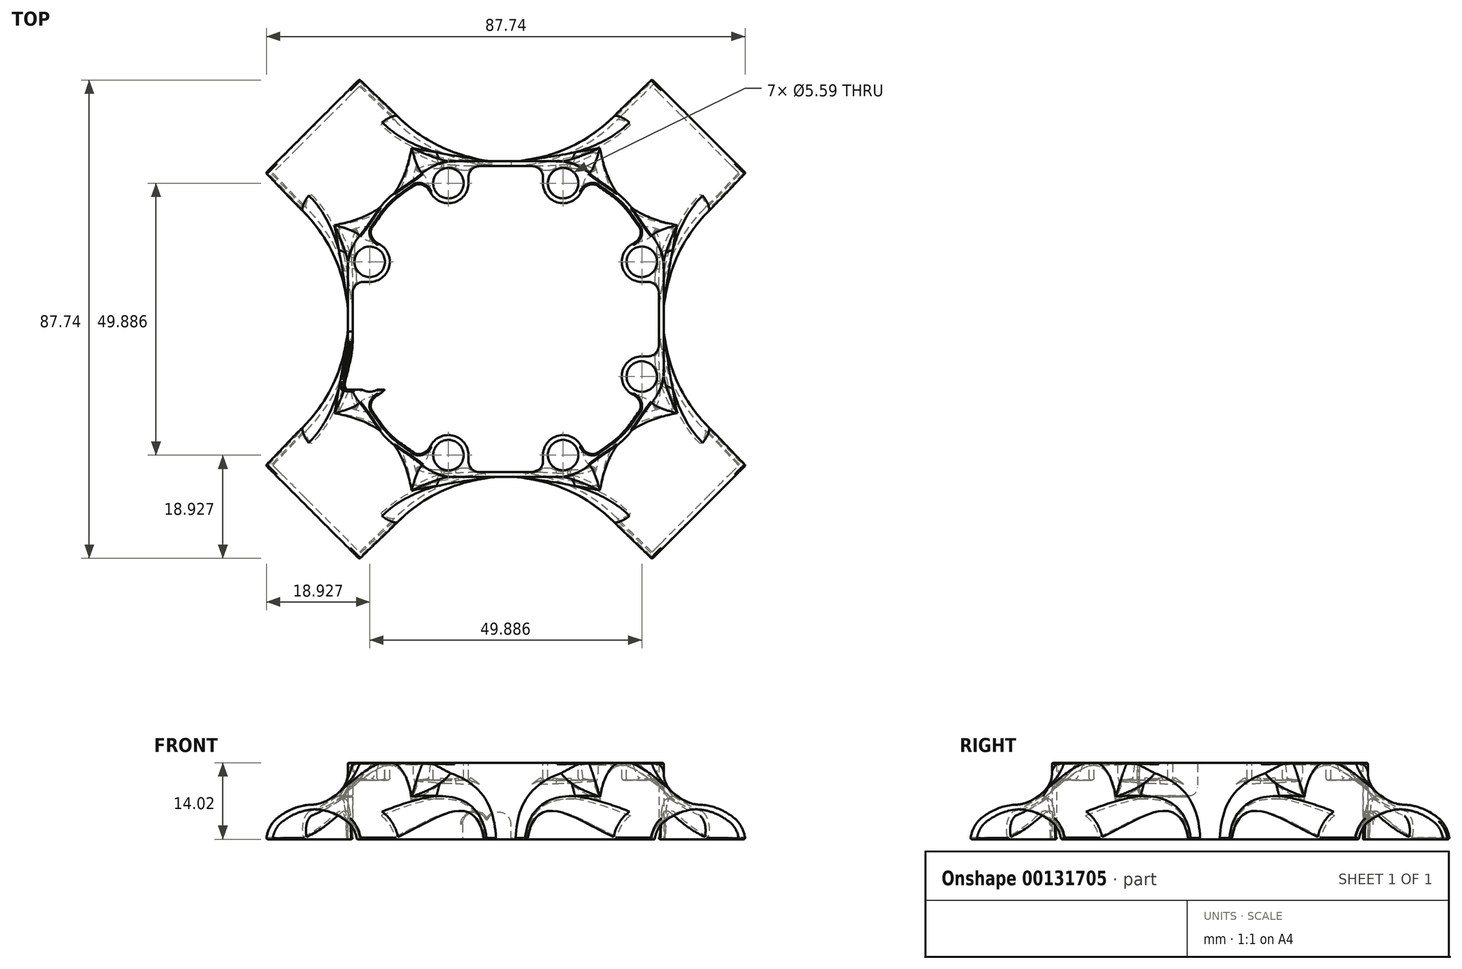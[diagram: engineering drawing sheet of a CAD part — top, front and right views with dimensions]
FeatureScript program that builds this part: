
annotation { "Feature Type Name" : "Feature", "Feature Type Description" : "" }
export const myFeature = defineFeature(function(context is Context, id is Id, definition is map)
    precondition{}
    {
        {
            var Q0;
            Q0=qCreatedBy(makeId("Top.planeOp"),FACE);
            var sketch = newSketch(context, id + "F0", { "sketchPlane" : qUnion([Q0])});
            skLineSegment(sketch, "E0.left", {"start": v(28.96, 12.57) * mm, "end": v(28.96, -12.57) * mm});
            skLineSegment(sketch, "E0.right", {"start": v(-28.96, 12.57) * mm, "end": v(-28.96, -12.57) * mm});
            skPoint(sketch, "E0.middle", {"position": v(0, 0) * mm});
            skLineSegment(sketch, "E1.bottom", {"start": v(12.57, 28.96) * mm, "end": v(-12.57, 28.96) * mm});
            skLineSegment(sketch, "E1.top", {"start": v(12.57, -28.96) * mm, "end": v(-12.57, -28.96) * mm});
            skArc(sketch, "E2", {"start": v(-28.96, 12.57) * mm, "mid": v(-20.01, 20.01) * mm, "end": v(-12.57, 28.96) * mm});
            skArc(sketch, "E3", {"start": v(12.57, 28.96) * mm, "mid": v(20.01, 20.01) * mm, "end": v(28.96, 12.57) * mm});
            skArc(sketch, "E4", {"start": v(28.96, -12.57) * mm, "mid": v(20.01, -20.01) * mm, "end": v(12.57, -28.96) * mm});
            skArc(sketch, "E5", {"start": v(-12.57, -28.96) * mm, "mid": v(-20.01, -20.01) * mm, "end": v(-28.96, -12.57) * mm});
            skSolve(sketch);
        }
        {
            var Q0;
            Q0=qCreatedBy(makeId("Top.planeOp"),FACE);
            cPlane(context, id + "F1", {"entities" : qUnion([Q0]), "cplaneType" : CPlaneType.OFFSET, "offset" : 14.02 * mm, "oppositeDirection" : true, "width" : 152.4 * mm, "height" : 152.4 * mm});
        }
        {
            var Q0;
            Q0=qCreatedBy(id+"F1.planeOp",FACE);
            var sketch = newSketch(context, id + "F2", { "sketchPlane" : qUnion([Q0])});
            skPoint(sketch, "E6.middle", {"position": v(0, 0) * mm});
            skArc(sketch, "E7", {"start": v(-37.14, -19.76) * mm, "mid": v(-28.96, 0) * mm, "end": v(-37.14, 19.76) * mm});
            skArc(sketch, "E8", {"start": v(-19.76, 37.14) * mm, "mid": v(0, 28.96) * mm, "end": v(19.76, 37.14) * mm});
            skArc(sketch, "E9", {"start": v(37.14, 19.76) * mm, "mid": v(28.96, 0) * mm, "end": v(37.14, -19.76) * mm});
            skArc(sketch, "E10", {"start": v(19.76, -37.14) * mm, "mid": v(0, -28.96) * mm, "end": v(-19.76, -37.14) * mm});
            skLineSegment(sketch, "E11", {"start": v(-44.09, 26.7) * mm, "end": v(-37.14, 19.76) * mm});
            skLineSegment(sketch, "E12", {"start": v(-19.76, 37.14) * mm, "end": v(-26.7, 44.09) * mm});
            skLineSegment(sketch, "E13", {"start": v(-26.7, 44.09) * mm, "end": v(-44.09, 26.7) * mm});
            skLineSegment(sketch, "E14", {"start": v(19.76, 37.14) * mm, "end": v(26.7, 44.09) * mm});
            skLineSegment(sketch, "E15", {"start": v(26.7, 44.09) * mm, "end": v(44.09, 26.7) * mm});
            skLineSegment(sketch, "E16", {"start": v(44.09, 26.7) * mm, "end": v(37.14, 19.76) * mm});
            skLineSegment(sketch, "E17", {"start": v(-19.76, -37.14) * mm, "end": v(-26.7, -44.09) * mm});
            skLineSegment(sketch, "E18", {"start": v(-26.7, -44.09) * mm, "end": v(-44.09, -26.7) * mm});
            skLineSegment(sketch, "E19", {"start": v(-44.09, -26.7) * mm, "end": v(-37.14, -19.76) * mm});
            skLineSegment(sketch, "E20", {"start": v(37.14, -19.76) * mm, "end": v(44.09, -26.7) * mm});
            skLineSegment(sketch, "E21", {"start": v(44.09, -26.7) * mm, "end": v(26.7, -44.09) * mm});
            skLineSegment(sketch, "E22", {"start": v(26.7, -44.09) * mm, "end": v(19.76, -37.14) * mm});
            skPoint(sketch, "E23.orphan", {"position": v(-29.11, 29.11) * mm});
            skPoint(sketch, "E24.orphan", {"position": v(29.1, 29.1) * mm});
            skPoint(sketch, "E25.orphan", {"position": v(29.11, -29.11) * mm});
            skPoint(sketch, "E26.orphan", {"position": v(-29.1, -29.1) * mm});
            skLineSegment(sketch, "E27.bottom", {"start": v(54.62, -53.7) * mm, "end": v(-54.62, -53.7) * mm});
            skLineSegment(sketch, "E27.top", {"start": v(54.62, 53.7) * mm, "end": v(-54.62, 53.7) * mm});
            skLineSegment(sketch, "E27.left", {"start": v(54.62, -53.7) * mm, "end": v(54.62, 53.7) * mm});
            skLineSegment(sketch, "E27.right", {"start": v(-54.62, -53.7) * mm, "end": v(-54.62, 53.7) * mm});
            skSolve(sketch);
        }
        {
            var Q0;
            Q0=makeQuery(id+"F0.imprint","IMPRINT",FACE,{"disambiguationData":[TD([[makeQuery(id+"F0.imprint","IMPRINT",EDGE,{"derivedFrom":sQuery(id+"F0.wireOp",EDGE,"E0.left")}),-1.0]])]});
            var Q1;
            Q1=qCreatedBy(id+"F1.planeOp",FACE);
            extrude(context, id + "F3", {"entities" : qUnion([Q0]), "endBound" : BoundingType.UP_TO_SURFACE, "oppositeDirection" : true, "endBoundEntityFace" : qUnion([Q1]), "depth" : 25.4 * mm});
        }
        {
            var Q0;
            Q0=makeQuery(id+"F0.imprint","IMPRINT",FACE,{"disambiguationData":[TD([[makeQuery(id+"F0.imprint","IMPRINT",EDGE,{"derivedFrom":sQuery(id+"F0.wireOp",EDGE,"E0.left")}),-1.0]])]});
            extrude(context, id + "F4", {"entities" : qUnion([Q0]), "operationType" : NewBodyOperationType.ADD, "depth" : 25.4 * mm});
        }
        {
            var Q0;
            Q0=qCreatedBy(id+"F1.planeOp",FACE);
            var sketch = newSketch(context, id + "F5", { "sketchPlane" : qUnion([Q0])});
            skLineSegment(sketch, "E28", {"start": v(-26.36, -26.36) * mm, "end": v(26.36, 26.36) * mm});
            skLineSegment(sketch, "E29", {"start": v(26.36, -26.36) * mm, "end": v(-26.36, 26.36) * mm});
            skSolve(sketch);
        }
        {
            var Q0;
            Q0=qCreatedBy(makeId("Front.planeOp"),FACE);
            var Q1;
            Q1=sQuery(id+"F5.wireOp",EDGE,"E28");
            cPlane(context, id + "F6", {"entities" : qUnion([Q0, Q1]), "cplaneType" : CPlaneType.LINE_ANGLE, "offset" : 25.4 * mm, "angle" : 0 * degree, "width" : 152.4 * mm, "height" : 152.4 * mm});
        }
        {
            var Q0;
            Q0=qCreatedBy(makeId("Front.planeOp"),FACE);
            var Q1;
            Q1=sQuery(id+"F5.wireOp",EDGE,"E29");
            cPlane(context, id + "F7", {"entities" : qUnion([Q0, Q1]), "cplaneType" : CPlaneType.LINE_ANGLE, "offset" : 25.4 * mm, "angle" : 0 * degree, "width" : 152.4 * mm, "height" : 152.4 * mm});
        }
        {
            var Q0;
            Q0=qCreatedBy(id+"F6.planeOp",FACE);
            var sketch = newSketch(context, id + "F8", { "sketchPlane" : qUnion([Q0])});
            skCircle(sketch, "E30", {"center": v(50.22, 20.65) * mm, "radius": 28.32 * mm});
            skLineSegment(sketch, "E31.bottom", {"start": v(50.22, 20.65) * mm, "end": v(12.75, 20.65) * mm});
            skLineSegment(sketch, "E31.top", {"start": v(50.22, -14.02) * mm, "end": v(12.75, -14.02) * mm});
            skLineSegment(sketch, "E31.left", {"start": v(50.22, 20.65) * mm, "end": v(50.22, -14.02) * mm});
            skLineSegment(sketch, "E31.right", {"start": v(12.75, 20.65) * mm, "end": v(12.75, -14.02) * mm});
            skCircle(sketch, "E32", {"center": v(-50.22, 20.65) * mm, "radius": 28.32 * mm});
            skLineSegment(sketch, "E33.bottom", {"start": v(-50.22, 20.65) * mm, "end": v(-12.75, 20.65) * mm});
            skLineSegment(sketch, "E33.top", {"start": v(-50.22, -14.02) * mm, "end": v(-12.75, -14.02) * mm});
            skLineSegment(sketch, "E33.left", {"start": v(-50.22, 20.65) * mm, "end": v(-50.22, -14.02) * mm});
            skLineSegment(sketch, "E33.right", {"start": v(-12.75, 20.65) * mm, "end": v(-12.75, -14.02) * mm});
            skSolve(sketch);
        }
        {
            var Q0;
            Q0=qCreatedBy(id+"F7.planeOp",FACE);
            var sketch = newSketch(context, id + "F9", { "sketchPlane" : qUnion([Q0])});
            skCircle(sketch, "E34", {"center": v(-50.22, 20.65) * mm, "radius": 28.32 * mm});
            skCircle(sketch, "E35", {"center": v(50.22, 20.65) * mm, "radius": 28.32 * mm});
            skLineSegment(sketch, "E36.bottom", {"start": v(-50.22, 20.65) * mm, "end": v(-12.75, 20.65) * mm});
            skLineSegment(sketch, "E36.top", {"start": v(-50.22, -14.02) * mm, "end": v(-12.75, -14.02) * mm});
            skLineSegment(sketch, "E36.left", {"start": v(-50.22, 20.65) * mm, "end": v(-50.22, -14.02) * mm});
            skLineSegment(sketch, "E36.right", {"start": v(-12.75, 20.65) * mm, "end": v(-12.75, -14.02) * mm});
            skLineSegment(sketch, "E37.bottom", {"start": v(50.22, 20.65) * mm, "end": v(12.75, 20.65) * mm});
            skLineSegment(sketch, "E37.top", {"start": v(50.22, -14.02) * mm, "end": v(12.75, -14.02) * mm});
            skLineSegment(sketch, "E37.left", {"start": v(50.22, 20.65) * mm, "end": v(50.22, -14.02) * mm});
            skLineSegment(sketch, "E37.right", {"start": v(12.75, 20.65) * mm, "end": v(12.75, -14.02) * mm});
            skSolve(sketch);
        }
        {
            var Q0;
            {var subQ1=sQuery(id+"F8.wireOp",EDGE,"E31.top");Q0=makeQuery(id+"F8.imprint","IMPRINT",FACE,{"disambiguationData":[TD([[makeQuery(id+"F8.imprint","IMPRINT",EDGE,{"derivedFrom":subQ1}),-1.0]])]});}
            var Q1;
            {var subQ1=sQuery(id+"F8.wireOp",EDGE,"E33.top");Q1=makeQuery(id+"F8.imprint","IMPRINT",FACE,{"disambiguationData":[TD([[makeQuery(id+"F8.imprint","IMPRINT",EDGE,{"derivedFrom":subQ1}),1.0]])]});}
            extrude(context, id + "F10", {"entities" : qUnion([Q0, Q1]), "operationType" : NewBodyOperationType.ADD, "endBound" : BoundingType.SYMMETRIC, "depth" : 38.1 * mm});
        }
        {
            var Q0;
            {var subQ1=sQuery(id+"F9.wireOp",EDGE,"E36.top");Q0=makeQuery(id+"F9.imprint","IMPRINT",FACE,{"disambiguationData":[TD([[makeQuery(id+"F9.imprint","IMPRINT",EDGE,{"derivedFrom":subQ1}),1.0]])]});}
            var Q1;
            {var subQ1=sQuery(id+"F9.wireOp",EDGE,"E37.top");Q1=makeQuery(id+"F9.imprint","IMPRINT",FACE,{"disambiguationData":[TD([[makeQuery(id+"F9.imprint","IMPRINT",EDGE,{"derivedFrom":subQ1}),-1.0]])]});}
            extrude(context, id + "F11", {"entities" : qUnion([Q0, Q1]), "operationType" : NewBodyOperationType.ADD, "endBound" : BoundingType.SYMMETRIC, "depth" : 38.1 * mm});
        }
        {
            var Q0;
            Q0=makeQuery(id+"F10.opExtrude","CAP_EDGE",EDGE,{"disambiguationData":[OSD([sQuery(id+"F8.wireOp",EDGE,"E30")])],"isStart":false});
            var Q1;
            Q1=makeQuery(id+"F10.opExtrude","CAP_EDGE",EDGE,{"disambiguationData":[OSD([sQuery(id+"F8.wireOp",EDGE,"E30")])],"isStart":true});
            var Q2;
            Q2=makeQuery(id+"F10.opExtrude","CAP_EDGE",EDGE,{"disambiguationData":[OSD([sQuery(id+"F8.wireOp",EDGE,"E32")])],"isStart":false});
            var Q3;
            Q3=makeQuery(id+"F10.opExtrude","CAP_EDGE",EDGE,{"disambiguationData":[OSD([sQuery(id+"F8.wireOp",EDGE,"E32")])],"isStart":true});
            var Q4;
            Q4=makeQuery(id+"F11.opExtrude","CAP_EDGE",EDGE,{"disambiguationData":[OSD([sQuery(id+"F9.wireOp",EDGE,"E35")])],"isStart":true});
            var Q5;
            Q5=makeQuery(id+"F11.opExtrude","CAP_EDGE",EDGE,{"disambiguationData":[OSD([sQuery(id+"F9.wireOp",EDGE,"E35")])],"isStart":false});
            var Q6;
            Q6=makeQuery(id+"F11.opExtrude","CAP_EDGE",EDGE,{"disambiguationData":[OSD([sQuery(id+"F9.wireOp",EDGE,"E34")])],"isStart":true});
            var Q7;
            Q7=makeQuery(id+"F11.opExtrude","CAP_EDGE",EDGE,{"disambiguationData":[OSD([sQuery(id+"F9.wireOp",EDGE,"E34")])],"isStart":false});
            fillet(context, id + "F12", {"entities" : qUnion([Q0, Q1, Q2, Q3, Q4, Q5, Q6, Q7]), "radius" : 19.05 * mm, "tangentPropagation" : true, "allowEdgeOverflow" : false});
        }
        {
            var Q0;
            Q0=makeQuery(id+"F2.imprint","IMPRINT",FACE,{"disambiguationData":[TD([[makeQuery(id+"F2.imprint","IMPRINT",EDGE,{"derivedFrom":sQuery(id+"F2.wireOp",EDGE,"E7")}),1.0]])]});
            extrude(context, id + "F13", {"entities" : qUnion([Q0]), "operationType" : NewBodyOperationType.REMOVE, "depth" : 50.8 * mm});
        }
        {
            var Q0;
            Q0=makeQuery(id+"F13.boolean.opBoolean","INTERSECT",EDGE,{"derivedFrom":[makeQuery(id+"F12.opFillet","BLEND_FACE",FACE,{"disambiguationData":[OSD([sQuery(id+"F8.wireOp",EDGE,"E30")])]}),makeQuery(id+"F13.opExtrude","SWEPT_FACE",FACE,{"disambiguationData":[OSD([sQuery(id+"F2.wireOp",EDGE,"E19")])]})]});
            var Q1;
            Q1=makeQuery(id+"F13.boolean.opBoolean","INTERSECT",EDGE,{"derivedFrom":[makeQuery(id+"F12.opFillet","BLEND_FACE",FACE,{"disambiguationData":[OSD([sQuery(id+"F8.wireOp",EDGE,"E30")])]}),makeQuery(id+"F13.opExtrude","SWEPT_FACE",FACE,{"disambiguationData":[OSD([sQuery(id+"F2.wireOp",EDGE,"E17")])]})]});
            var Q2;
            Q2=makeQuery(id+"F13.boolean.opBoolean","INTERSECT",EDGE,{"derivedFrom":[makeQuery(id+"F12.opFillet","BLEND_FACE",FACE,{"disambiguationData":[OSD([sQuery(id+"F8.wireOp",EDGE,"E32")])]}),makeQuery(id+"F13.opExtrude","SWEPT_FACE",FACE,{"disambiguationData":[OSD([sQuery(id+"F2.wireOp",EDGE,"E14")])]})]});
            var Q3;
            Q3=makeQuery(id+"F13.boolean.opBoolean","INTERSECT",EDGE,{"derivedFrom":[makeQuery(id+"F12.opFillet","BLEND_FACE",FACE,{"disambiguationData":[OSD([sQuery(id+"F8.wireOp",EDGE,"E32")])]}),makeQuery(id+"F13.opExtrude","SWEPT_FACE",FACE,{"disambiguationData":[OSD([sQuery(id+"F2.wireOp",EDGE,"E16")])]})]});
            var Q4;
            Q4=makeQuery(id+"F13.boolean.opBoolean","INTERSECT",EDGE,{"derivedFrom":[makeQuery(id+"F12.opFillet","BLEND_FACE",FACE,{"disambiguationData":[OSD([sQuery(id+"F9.wireOp",EDGE,"E35")])]}),makeQuery(id+"F13.opExtrude","SWEPT_FACE",FACE,{"disambiguationData":[OSD([sQuery(id+"F2.wireOp",EDGE,"E11")])]})]});
            var Q5;
            Q5=makeQuery(id+"F13.boolean.opBoolean","INTERSECT",EDGE,{"derivedFrom":[makeQuery(id+"F12.opFillet","BLEND_FACE",FACE,{"disambiguationData":[OSD([sQuery(id+"F9.wireOp",EDGE,"E35")])]}),makeQuery(id+"F13.opExtrude","SWEPT_FACE",FACE,{"disambiguationData":[OSD([sQuery(id+"F2.wireOp",EDGE,"E12")])]})]});
            var Q6;
            Q6=makeQuery(id+"F13.boolean.opBoolean","INTERSECT",EDGE,{"derivedFrom":[makeQuery(id+"F12.opFillet","BLEND_FACE",FACE,{"disambiguationData":[OSD([sQuery(id+"F9.wireOp",EDGE,"E34")])]}),makeQuery(id+"F13.opExtrude","SWEPT_FACE",FACE,{"disambiguationData":[OSD([sQuery(id+"F2.wireOp",EDGE,"E22")])]})]});
            var Q7;
            Q7=makeQuery(id+"F13.boolean.opBoolean","INTERSECT",EDGE,{"derivedFrom":[makeQuery(id+"F12.opFillet","BLEND_FACE",FACE,{"disambiguationData":[OSD([sQuery(id+"F9.wireOp",EDGE,"E34")])]}),makeQuery(id+"F13.opExtrude","SWEPT_FACE",FACE,{"disambiguationData":[OSD([sQuery(id+"F2.wireOp",EDGE,"E20")])]})]});
            fillet(context, id + "F14", {"entities" : qUnion([Q0, Q1, Q2, Q3, Q4, Q5, Q6, Q7]), "radius" : 5.6 * mm, "tangentPropagation" : true, "allowEdgeOverflow" : false});
        }
        {
            var Q0;
            {var subQ0=sQuery(id+"F0.wireOp",EDGE,"E5");Q0=makeQuery(id+"F12.opFillet","BLEND_EDGE",EDGE,{"blendedFrom":[makeQuery(id+"F10.opExtrude","CAP_EDGE",EDGE,{"disambiguationData":[OSD([sQuery(id+"F8.wireOp",EDGE,"E30")])],"isStart":false}),makeQuery(id+"F4.boolean.opBoolean","MERGE",FACE,{"derivedFrom":[makeQuery(id+"F3.opExtrude","SWEPT_FACE",FACE,{"disambiguationData":[OSD([subQ0])]}),makeQuery(id+"F4.opExtrude","SWEPT_FACE",FACE,{"disambiguationData":[OSD([subQ0])]})]})],"blendedInto":[makeQuery(id+"F4.boolean.opBoolean","MERGE",FACE,{"derivedFrom":[makeQuery(id+"F3.opExtrude","SWEPT_FACE",FACE,{"disambiguationData":[OSD([subQ0])]}),makeQuery(id+"F4.opExtrude","SWEPT_FACE",FACE,{"disambiguationData":[OSD([subQ0])]})]})]});}
            var Q1;
            {var subQ0=sQuery(id+"F0.wireOp",EDGE,"E0.right");Q1=makeQuery(id+"F12.opFillet","BLEND_EDGE",EDGE,{"blendedFrom":[makeQuery(id+"F10.opExtrude","CAP_EDGE",EDGE,{"disambiguationData":[OSD([sQuery(id+"F8.wireOp",EDGE,"E30")])],"isStart":false}),makeQuery(id+"F4.boolean.opBoolean","MERGE",FACE,{"derivedFrom":[makeQuery(id+"F3.opExtrude","SWEPT_FACE",FACE,{"disambiguationData":[OSD([subQ0])]}),makeQuery(id+"F4.opExtrude","SWEPT_FACE",FACE,{"disambiguationData":[OSD([subQ0])]})]})],"blendedInto":[makeQuery(id+"F4.boolean.opBoolean","MERGE",FACE,{"derivedFrom":[makeQuery(id+"F3.opExtrude","SWEPT_FACE",FACE,{"disambiguationData":[OSD([subQ0])]}),makeQuery(id+"F4.opExtrude","SWEPT_FACE",FACE,{"disambiguationData":[OSD([subQ0])]})]})]});}
            var Q2;
            {var subQ0=sQuery(id+"F0.wireOp",EDGE,"E1.top");Q2=makeQuery(id+"F12.opFillet","BLEND_EDGE",EDGE,{"blendedFrom":[makeQuery(id+"F10.opExtrude","CAP_EDGE",EDGE,{"disambiguationData":[OSD([sQuery(id+"F8.wireOp",EDGE,"E30")])],"isStart":true}),makeQuery(id+"F4.boolean.opBoolean","MERGE",FACE,{"derivedFrom":[makeQuery(id+"F3.opExtrude","SWEPT_FACE",FACE,{"disambiguationData":[OSD([subQ0])]}),makeQuery(id+"F4.opExtrude","SWEPT_FACE",FACE,{"disambiguationData":[OSD([subQ0])]})]})],"blendedInto":[makeQuery(id+"F4.boolean.opBoolean","MERGE",FACE,{"derivedFrom":[makeQuery(id+"F3.opExtrude","SWEPT_FACE",FACE,{"disambiguationData":[OSD([subQ0])]}),makeQuery(id+"F4.opExtrude","SWEPT_FACE",FACE,{"disambiguationData":[OSD([subQ0])]})]})]});}
            var Q3;
            {var subQ0=sQuery(id+"F0.wireOp",EDGE,"E1.bottom");Q3=makeQuery(id+"F12.opFillet","BLEND_EDGE",EDGE,{"blendedFrom":[makeQuery(id+"F10.opExtrude","CAP_EDGE",EDGE,{"disambiguationData":[OSD([sQuery(id+"F8.wireOp",EDGE,"E32")])],"isStart":false}),makeQuery(id+"F4.boolean.opBoolean","MERGE",FACE,{"derivedFrom":[makeQuery(id+"F3.opExtrude","SWEPT_FACE",FACE,{"disambiguationData":[OSD([subQ0])]}),makeQuery(id+"F4.opExtrude","SWEPT_FACE",FACE,{"disambiguationData":[OSD([subQ0])]})]})],"blendedInto":[makeQuery(id+"F4.boolean.opBoolean","MERGE",FACE,{"derivedFrom":[makeQuery(id+"F3.opExtrude","SWEPT_FACE",FACE,{"disambiguationData":[OSD([subQ0])]}),makeQuery(id+"F4.opExtrude","SWEPT_FACE",FACE,{"disambiguationData":[OSD([subQ0])]})]})]});}
            var Q4;
            {var subQ0=sQuery(id+"F0.wireOp",EDGE,"E3");Q4=makeQuery(id+"F12.opFillet","BLEND_EDGE",EDGE,{"blendedFrom":[makeQuery(id+"F10.opExtrude","CAP_EDGE",EDGE,{"disambiguationData":[OSD([sQuery(id+"F8.wireOp",EDGE,"E32")])],"isStart":false}),makeQuery(id+"F4.boolean.opBoolean","MERGE",FACE,{"derivedFrom":[makeQuery(id+"F3.opExtrude","SWEPT_FACE",FACE,{"disambiguationData":[OSD([subQ0])]}),makeQuery(id+"F4.opExtrude","SWEPT_FACE",FACE,{"disambiguationData":[OSD([subQ0])]})]})],"blendedInto":[makeQuery(id+"F4.boolean.opBoolean","MERGE",FACE,{"derivedFrom":[makeQuery(id+"F3.opExtrude","SWEPT_FACE",FACE,{"disambiguationData":[OSD([subQ0])]}),makeQuery(id+"F4.opExtrude","SWEPT_FACE",FACE,{"disambiguationData":[OSD([subQ0])]})]})]});}
            var Q5;
            {var subQ0=sQuery(id+"F0.wireOp",EDGE,"E0.left");Q5=makeQuery(id+"F12.opFillet","BLEND_EDGE",EDGE,{"blendedFrom":[makeQuery(id+"F10.opExtrude","CAP_EDGE",EDGE,{"disambiguationData":[OSD([sQuery(id+"F8.wireOp",EDGE,"E32")])],"isStart":true}),makeQuery(id+"F4.boolean.opBoolean","MERGE",FACE,{"derivedFrom":[makeQuery(id+"F3.opExtrude","SWEPT_FACE",FACE,{"disambiguationData":[OSD([subQ0])]}),makeQuery(id+"F4.opExtrude","SWEPT_FACE",FACE,{"disambiguationData":[OSD([subQ0])]})]})],"blendedInto":[makeQuery(id+"F4.boolean.opBoolean","MERGE",FACE,{"derivedFrom":[makeQuery(id+"F3.opExtrude","SWEPT_FACE",FACE,{"disambiguationData":[OSD([subQ0])]}),makeQuery(id+"F4.opExtrude","SWEPT_FACE",FACE,{"disambiguationData":[OSD([subQ0])]})]})]});}
            var Q6;
            {var subQ0=sQuery(id+"F0.wireOp",EDGE,"E0.right");Q6=makeQuery(id+"F12.opFillet","BLEND_EDGE",EDGE,{"blendedFrom":[makeQuery(id+"F11.opExtrude","CAP_EDGE",EDGE,{"disambiguationData":[OSD([sQuery(id+"F9.wireOp",EDGE,"E35")])],"isStart":true}),makeQuery(id+"F4.boolean.opBoolean","MERGE",FACE,{"derivedFrom":[makeQuery(id+"F3.opExtrude","SWEPT_FACE",FACE,{"disambiguationData":[OSD([subQ0])]}),makeQuery(id+"F4.opExtrude","SWEPT_FACE",FACE,{"disambiguationData":[OSD([subQ0])]})]})],"blendedInto":[makeQuery(id+"F4.boolean.opBoolean","MERGE",FACE,{"derivedFrom":[makeQuery(id+"F3.opExtrude","SWEPT_FACE",FACE,{"disambiguationData":[OSD([subQ0])]}),makeQuery(id+"F4.opExtrude","SWEPT_FACE",FACE,{"disambiguationData":[OSD([subQ0])]})]})]});}
            var Q7;
            {var subQ0=sQuery(id+"F0.wireOp",EDGE,"E2");Q7=makeQuery(id+"F12.opFillet","BLEND_EDGE",EDGE,{"blendedFrom":[makeQuery(id+"F11.opExtrude","CAP_EDGE",EDGE,{"disambiguationData":[OSD([sQuery(id+"F9.wireOp",EDGE,"E35")])],"isStart":true}),makeQuery(id+"F4.boolean.opBoolean","MERGE",FACE,{"derivedFrom":[makeQuery(id+"F3.opExtrude","SWEPT_FACE",FACE,{"disambiguationData":[OSD([subQ0])]}),makeQuery(id+"F4.opExtrude","SWEPT_FACE",FACE,{"disambiguationData":[OSD([subQ0])]})]})],"blendedInto":[makeQuery(id+"F4.boolean.opBoolean","MERGE",FACE,{"derivedFrom":[makeQuery(id+"F3.opExtrude","SWEPT_FACE",FACE,{"disambiguationData":[OSD([subQ0])]}),makeQuery(id+"F4.opExtrude","SWEPT_FACE",FACE,{"disambiguationData":[OSD([subQ0])]})]})]});}
            var Q8;
            {var subQ0=sQuery(id+"F0.wireOp",EDGE,"E1.bottom");Q8=makeQuery(id+"F12.opFillet","BLEND_EDGE",EDGE,{"blendedFrom":[makeQuery(id+"F11.opExtrude","CAP_EDGE",EDGE,{"disambiguationData":[OSD([sQuery(id+"F9.wireOp",EDGE,"E35")])],"isStart":false}),makeQuery(id+"F4.boolean.opBoolean","MERGE",FACE,{"derivedFrom":[makeQuery(id+"F3.opExtrude","SWEPT_FACE",FACE,{"disambiguationData":[OSD([subQ0])]}),makeQuery(id+"F4.opExtrude","SWEPT_FACE",FACE,{"disambiguationData":[OSD([subQ0])]})]})],"blendedInto":[makeQuery(id+"F4.boolean.opBoolean","MERGE",FACE,{"derivedFrom":[makeQuery(id+"F3.opExtrude","SWEPT_FACE",FACE,{"disambiguationData":[OSD([subQ0])]}),makeQuery(id+"F4.opExtrude","SWEPT_FACE",FACE,{"disambiguationData":[OSD([subQ0])]})]})]});}
            var Q9;
            {var subQ0=sQuery(id+"F0.wireOp",EDGE,"E0.left");Q9=makeQuery(id+"F12.opFillet","BLEND_EDGE",EDGE,{"blendedFrom":[makeQuery(id+"F11.opExtrude","CAP_EDGE",EDGE,{"disambiguationData":[OSD([sQuery(id+"F9.wireOp",EDGE,"E34")])],"isStart":false}),makeQuery(id+"F4.boolean.opBoolean","MERGE",FACE,{"derivedFrom":[makeQuery(id+"F3.opExtrude","SWEPT_FACE",FACE,{"disambiguationData":[OSD([subQ0])]}),makeQuery(id+"F4.opExtrude","SWEPT_FACE",FACE,{"disambiguationData":[OSD([subQ0])]})]})],"blendedInto":[makeQuery(id+"F4.boolean.opBoolean","MERGE",FACE,{"derivedFrom":[makeQuery(id+"F3.opExtrude","SWEPT_FACE",FACE,{"disambiguationData":[OSD([subQ0])]}),makeQuery(id+"F4.opExtrude","SWEPT_FACE",FACE,{"disambiguationData":[OSD([subQ0])]})]})]});}
            var Q10;
            {var subQ0=sQuery(id+"F0.wireOp",EDGE,"E4");Q10=makeQuery(id+"F12.opFillet","BLEND_EDGE",EDGE,{"blendedFrom":[makeQuery(id+"F11.opExtrude","CAP_EDGE",EDGE,{"disambiguationData":[OSD([sQuery(id+"F9.wireOp",EDGE,"E34")])],"isStart":false}),makeQuery(id+"F4.boolean.opBoolean","MERGE",FACE,{"derivedFrom":[makeQuery(id+"F3.opExtrude","SWEPT_FACE",FACE,{"disambiguationData":[OSD([subQ0])]}),makeQuery(id+"F4.opExtrude","SWEPT_FACE",FACE,{"disambiguationData":[OSD([subQ0])]})]})],"blendedInto":[makeQuery(id+"F4.boolean.opBoolean","MERGE",FACE,{"derivedFrom":[makeQuery(id+"F3.opExtrude","SWEPT_FACE",FACE,{"disambiguationData":[OSD([subQ0])]}),makeQuery(id+"F4.opExtrude","SWEPT_FACE",FACE,{"disambiguationData":[OSD([subQ0])]})]})]});}
            var Q11;
            {var subQ0=sQuery(id+"F0.wireOp",EDGE,"E1.top");Q11=makeQuery(id+"F12.opFillet","BLEND_EDGE",EDGE,{"blendedFrom":[makeQuery(id+"F11.opExtrude","CAP_EDGE",EDGE,{"disambiguationData":[OSD([sQuery(id+"F9.wireOp",EDGE,"E34")])],"isStart":true}),makeQuery(id+"F4.boolean.opBoolean","MERGE",FACE,{"derivedFrom":[makeQuery(id+"F3.opExtrude","SWEPT_FACE",FACE,{"disambiguationData":[OSD([subQ0])]}),makeQuery(id+"F4.opExtrude","SWEPT_FACE",FACE,{"disambiguationData":[OSD([subQ0])]})]})],"blendedInto":[makeQuery(id+"F4.boolean.opBoolean","MERGE",FACE,{"derivedFrom":[makeQuery(id+"F3.opExtrude","SWEPT_FACE",FACE,{"disambiguationData":[OSD([subQ0])]}),makeQuery(id+"F4.opExtrude","SWEPT_FACE",FACE,{"disambiguationData":[OSD([subQ0])]})]})]});}
            fillet(context, id + "F15", {"entities" : qUnion([Q0, Q1, Q2, Q3, Q4, Q5, Q6, Q7, Q8, Q9, Q10, Q11]), "radius" : 7.62 * mm, "tangentPropagation" : true, "allowEdgeOverflow" : false});
        }
        {
            var Q0;
            {var subQ0=sQuery(id+"F0.wireOp",EDGE,"E0.right");var subQ1=makeQuery(id+"F10.opExtrude","CAP_EDGE",EDGE,{"disambiguationData":[OSD([sQuery(id+"F8.wireOp",EDGE,"E30")])],"isStart":false});var subQ2=sQuery(id+"F0.wireOp",EDGE,"E5");Q0=makeQuery(id+"F15.opFillet","BLEND_EDGE",EDGE,{"blendedFrom":[makeQuery(id+"F12.opFillet","BLEND_EDGE",EDGE,{"blendedFrom":[subQ1,makeQuery(id+"F4.boolean.opBoolean","MERGE",FACE,{"derivedFrom":[makeQuery(id+"F3.opExtrude","SWEPT_FACE",FACE,{"disambiguationData":[OSD([subQ2])]}),makeQuery(id+"F4.opExtrude","SWEPT_FACE",FACE,{"disambiguationData":[OSD([subQ2])]})]})],"blendedInto":[makeQuery(id+"F4.boolean.opBoolean","MERGE",FACE,{"derivedFrom":[makeQuery(id+"F3.opExtrude","SWEPT_FACE",FACE,{"disambiguationData":[OSD([subQ2])]}),makeQuery(id+"F4.opExtrude","SWEPT_FACE",FACE,{"disambiguationData":[OSD([subQ2])]})]})]}),makeQuery(id+"F12.opFillet","BLEND_EDGE",EDGE,{"blendedFrom":[subQ1,makeQuery(id+"F4.boolean.opBoolean","MERGE",FACE,{"derivedFrom":[makeQuery(id+"F3.opExtrude","SWEPT_FACE",FACE,{"disambiguationData":[OSD([subQ0])]}),makeQuery(id+"F4.opExtrude","SWEPT_FACE",FACE,{"disambiguationData":[OSD([subQ0])]})]})],"blendedInto":[makeQuery(id+"F4.boolean.opBoolean","MERGE",FACE,{"derivedFrom":[makeQuery(id+"F3.opExtrude","SWEPT_FACE",FACE,{"disambiguationData":[OSD([subQ0])]}),makeQuery(id+"F4.opExtrude","SWEPT_FACE",FACE,{"disambiguationData":[OSD([subQ0])]})]})]})],"blendedInto":[]});}
            var Q1;
            {var subQ0=sQuery(id+"F0.wireOp",EDGE,"E1.top");var subQ1=makeQuery(id+"F10.opExtrude","CAP_EDGE",EDGE,{"disambiguationData":[OSD([sQuery(id+"F8.wireOp",EDGE,"E30")])],"isStart":true});var subQ2=sQuery(id+"F0.wireOp",EDGE,"E5");Q1=makeQuery(id+"F15.opFillet","BLEND_EDGE",EDGE,{"blendedFrom":[makeQuery(id+"F12.opFillet","BLEND_EDGE",EDGE,{"blendedFrom":[subQ1,makeQuery(id+"F4.boolean.opBoolean","MERGE",FACE,{"derivedFrom":[makeQuery(id+"F3.opExtrude","SWEPT_FACE",FACE,{"disambiguationData":[OSD([subQ2])]}),makeQuery(id+"F4.opExtrude","SWEPT_FACE",FACE,{"disambiguationData":[OSD([subQ2])]})]})],"blendedInto":[makeQuery(id+"F4.boolean.opBoolean","MERGE",FACE,{"derivedFrom":[makeQuery(id+"F3.opExtrude","SWEPT_FACE",FACE,{"disambiguationData":[OSD([subQ2])]}),makeQuery(id+"F4.opExtrude","SWEPT_FACE",FACE,{"disambiguationData":[OSD([subQ2])]})]})]}),makeQuery(id+"F12.opFillet","BLEND_EDGE",EDGE,{"blendedFrom":[subQ1,makeQuery(id+"F4.boolean.opBoolean","MERGE",FACE,{"derivedFrom":[makeQuery(id+"F3.opExtrude","SWEPT_FACE",FACE,{"disambiguationData":[OSD([subQ0])]}),makeQuery(id+"F4.opExtrude","SWEPT_FACE",FACE,{"disambiguationData":[OSD([subQ0])]})]})],"blendedInto":[makeQuery(id+"F4.boolean.opBoolean","MERGE",FACE,{"derivedFrom":[makeQuery(id+"F3.opExtrude","SWEPT_FACE",FACE,{"disambiguationData":[OSD([subQ0])]}),makeQuery(id+"F4.opExtrude","SWEPT_FACE",FACE,{"disambiguationData":[OSD([subQ0])]})]})]})],"blendedInto":[]});}
            var Q2;
            {var subQ0=sQuery(id+"F0.wireOp",EDGE,"E1.bottom");var subQ1=makeQuery(id+"F10.opExtrude","CAP_EDGE",EDGE,{"disambiguationData":[OSD([sQuery(id+"F8.wireOp",EDGE,"E32")])],"isStart":false});var subQ2=sQuery(id+"F0.wireOp",EDGE,"E3");Q2=makeQuery(id+"F15.opFillet","BLEND_EDGE",EDGE,{"blendedFrom":[makeQuery(id+"F12.opFillet","BLEND_EDGE",EDGE,{"blendedFrom":[subQ1,makeQuery(id+"F4.boolean.opBoolean","MERGE",FACE,{"derivedFrom":[makeQuery(id+"F3.opExtrude","SWEPT_FACE",FACE,{"disambiguationData":[OSD([subQ2])]}),makeQuery(id+"F4.opExtrude","SWEPT_FACE",FACE,{"disambiguationData":[OSD([subQ2])]})]})],"blendedInto":[makeQuery(id+"F4.boolean.opBoolean","MERGE",FACE,{"derivedFrom":[makeQuery(id+"F3.opExtrude","SWEPT_FACE",FACE,{"disambiguationData":[OSD([subQ2])]}),makeQuery(id+"F4.opExtrude","SWEPT_FACE",FACE,{"disambiguationData":[OSD([subQ2])]})]})]}),makeQuery(id+"F12.opFillet","BLEND_EDGE",EDGE,{"blendedFrom":[subQ1,makeQuery(id+"F4.boolean.opBoolean","MERGE",FACE,{"derivedFrom":[makeQuery(id+"F3.opExtrude","SWEPT_FACE",FACE,{"disambiguationData":[OSD([subQ0])]}),makeQuery(id+"F4.opExtrude","SWEPT_FACE",FACE,{"disambiguationData":[OSD([subQ0])]})]})],"blendedInto":[makeQuery(id+"F4.boolean.opBoolean","MERGE",FACE,{"derivedFrom":[makeQuery(id+"F3.opExtrude","SWEPT_FACE",FACE,{"disambiguationData":[OSD([subQ0])]}),makeQuery(id+"F4.opExtrude","SWEPT_FACE",FACE,{"disambiguationData":[OSD([subQ0])]})]})]})],"blendedInto":[]});}
            var Q3;
            {var subQ0=sQuery(id+"F0.wireOp",EDGE,"E0.left");var subQ1=makeQuery(id+"F10.opExtrude","CAP_EDGE",EDGE,{"disambiguationData":[OSD([sQuery(id+"F8.wireOp",EDGE,"E32")])],"isStart":true});var subQ2=sQuery(id+"F0.wireOp",EDGE,"E3");Q3=makeQuery(id+"F15.opFillet","BLEND_EDGE",EDGE,{"blendedFrom":[makeQuery(id+"F12.opFillet","BLEND_EDGE",EDGE,{"blendedFrom":[subQ1,makeQuery(id+"F4.boolean.opBoolean","MERGE",FACE,{"derivedFrom":[makeQuery(id+"F3.opExtrude","SWEPT_FACE",FACE,{"disambiguationData":[OSD([subQ2])]}),makeQuery(id+"F4.opExtrude","SWEPT_FACE",FACE,{"disambiguationData":[OSD([subQ2])]})]})],"blendedInto":[makeQuery(id+"F4.boolean.opBoolean","MERGE",FACE,{"derivedFrom":[makeQuery(id+"F3.opExtrude","SWEPT_FACE",FACE,{"disambiguationData":[OSD([subQ2])]}),makeQuery(id+"F4.opExtrude","SWEPT_FACE",FACE,{"disambiguationData":[OSD([subQ2])]})]})]}),makeQuery(id+"F12.opFillet","BLEND_EDGE",EDGE,{"blendedFrom":[subQ1,makeQuery(id+"F4.boolean.opBoolean","MERGE",FACE,{"derivedFrom":[makeQuery(id+"F3.opExtrude","SWEPT_FACE",FACE,{"disambiguationData":[OSD([subQ0])]}),makeQuery(id+"F4.opExtrude","SWEPT_FACE",FACE,{"disambiguationData":[OSD([subQ0])]})]})],"blendedInto":[makeQuery(id+"F4.boolean.opBoolean","MERGE",FACE,{"derivedFrom":[makeQuery(id+"F3.opExtrude","SWEPT_FACE",FACE,{"disambiguationData":[OSD([subQ0])]}),makeQuery(id+"F4.opExtrude","SWEPT_FACE",FACE,{"disambiguationData":[OSD([subQ0])]})]})]})],"blendedInto":[]});}
            var Q4;
            {var subQ0=sQuery(id+"F0.wireOp",EDGE,"E0.right");var subQ1=makeQuery(id+"F11.opExtrude","CAP_EDGE",EDGE,{"disambiguationData":[OSD([sQuery(id+"F9.wireOp",EDGE,"E35")])],"isStart":true});var subQ2=sQuery(id+"F0.wireOp",EDGE,"E2");Q4=makeQuery(id+"F15.opFillet","BLEND_EDGE",EDGE,{"blendedFrom":[makeQuery(id+"F12.opFillet","BLEND_EDGE",EDGE,{"blendedFrom":[subQ1,makeQuery(id+"F4.boolean.opBoolean","MERGE",FACE,{"derivedFrom":[makeQuery(id+"F3.opExtrude","SWEPT_FACE",FACE,{"disambiguationData":[OSD([subQ2])]}),makeQuery(id+"F4.opExtrude","SWEPT_FACE",FACE,{"disambiguationData":[OSD([subQ2])]})]})],"blendedInto":[makeQuery(id+"F4.boolean.opBoolean","MERGE",FACE,{"derivedFrom":[makeQuery(id+"F3.opExtrude","SWEPT_FACE",FACE,{"disambiguationData":[OSD([subQ2])]}),makeQuery(id+"F4.opExtrude","SWEPT_FACE",FACE,{"disambiguationData":[OSD([subQ2])]})]})]}),makeQuery(id+"F12.opFillet","BLEND_EDGE",EDGE,{"blendedFrom":[subQ1,makeQuery(id+"F4.boolean.opBoolean","MERGE",FACE,{"derivedFrom":[makeQuery(id+"F3.opExtrude","SWEPT_FACE",FACE,{"disambiguationData":[OSD([subQ0])]}),makeQuery(id+"F4.opExtrude","SWEPT_FACE",FACE,{"disambiguationData":[OSD([subQ0])]})]})],"blendedInto":[makeQuery(id+"F4.boolean.opBoolean","MERGE",FACE,{"derivedFrom":[makeQuery(id+"F3.opExtrude","SWEPT_FACE",FACE,{"disambiguationData":[OSD([subQ0])]}),makeQuery(id+"F4.opExtrude","SWEPT_FACE",FACE,{"disambiguationData":[OSD([subQ0])]})]})]})],"blendedInto":[]});}
            var Q5;
            {var subQ0=sQuery(id+"F0.wireOp",EDGE,"E1.bottom");var subQ1=makeQuery(id+"F11.opExtrude","CAP_EDGE",EDGE,{"disambiguationData":[OSD([sQuery(id+"F9.wireOp",EDGE,"E35")])],"isStart":false});var subQ2=sQuery(id+"F0.wireOp",EDGE,"E2");Q5=makeQuery(id+"F15.opFillet","BLEND_EDGE",EDGE,{"blendedFrom":[makeQuery(id+"F12.opFillet","BLEND_EDGE",EDGE,{"blendedFrom":[subQ1,makeQuery(id+"F4.boolean.opBoolean","MERGE",FACE,{"derivedFrom":[makeQuery(id+"F3.opExtrude","SWEPT_FACE",FACE,{"disambiguationData":[OSD([subQ2])]}),makeQuery(id+"F4.opExtrude","SWEPT_FACE",FACE,{"disambiguationData":[OSD([subQ2])]})]})],"blendedInto":[makeQuery(id+"F4.boolean.opBoolean","MERGE",FACE,{"derivedFrom":[makeQuery(id+"F3.opExtrude","SWEPT_FACE",FACE,{"disambiguationData":[OSD([subQ2])]}),makeQuery(id+"F4.opExtrude","SWEPT_FACE",FACE,{"disambiguationData":[OSD([subQ2])]})]})]}),makeQuery(id+"F12.opFillet","BLEND_EDGE",EDGE,{"blendedFrom":[subQ1,makeQuery(id+"F4.boolean.opBoolean","MERGE",FACE,{"derivedFrom":[makeQuery(id+"F3.opExtrude","SWEPT_FACE",FACE,{"disambiguationData":[OSD([subQ0])]}),makeQuery(id+"F4.opExtrude","SWEPT_FACE",FACE,{"disambiguationData":[OSD([subQ0])]})]})],"blendedInto":[makeQuery(id+"F4.boolean.opBoolean","MERGE",FACE,{"derivedFrom":[makeQuery(id+"F3.opExtrude","SWEPT_FACE",FACE,{"disambiguationData":[OSD([subQ0])]}),makeQuery(id+"F4.opExtrude","SWEPT_FACE",FACE,{"disambiguationData":[OSD([subQ0])]})]})]})],"blendedInto":[]});}
            var Q6;
            {var subQ0=sQuery(id+"F0.wireOp",EDGE,"E0.left");var subQ1=makeQuery(id+"F11.opExtrude","CAP_EDGE",EDGE,{"disambiguationData":[OSD([sQuery(id+"F9.wireOp",EDGE,"E34")])],"isStart":false});var subQ2=sQuery(id+"F0.wireOp",EDGE,"E4");Q6=makeQuery(id+"F15.opFillet","BLEND_EDGE",EDGE,{"blendedFrom":[makeQuery(id+"F12.opFillet","BLEND_EDGE",EDGE,{"blendedFrom":[subQ1,makeQuery(id+"F4.boolean.opBoolean","MERGE",FACE,{"derivedFrom":[makeQuery(id+"F3.opExtrude","SWEPT_FACE",FACE,{"disambiguationData":[OSD([subQ2])]}),makeQuery(id+"F4.opExtrude","SWEPT_FACE",FACE,{"disambiguationData":[OSD([subQ2])]})]})],"blendedInto":[makeQuery(id+"F4.boolean.opBoolean","MERGE",FACE,{"derivedFrom":[makeQuery(id+"F3.opExtrude","SWEPT_FACE",FACE,{"disambiguationData":[OSD([subQ2])]}),makeQuery(id+"F4.opExtrude","SWEPT_FACE",FACE,{"disambiguationData":[OSD([subQ2])]})]})]}),makeQuery(id+"F12.opFillet","BLEND_EDGE",EDGE,{"blendedFrom":[subQ1,makeQuery(id+"F4.boolean.opBoolean","MERGE",FACE,{"derivedFrom":[makeQuery(id+"F3.opExtrude","SWEPT_FACE",FACE,{"disambiguationData":[OSD([subQ0])]}),makeQuery(id+"F4.opExtrude","SWEPT_FACE",FACE,{"disambiguationData":[OSD([subQ0])]})]})],"blendedInto":[makeQuery(id+"F4.boolean.opBoolean","MERGE",FACE,{"derivedFrom":[makeQuery(id+"F3.opExtrude","SWEPT_FACE",FACE,{"disambiguationData":[OSD([subQ0])]}),makeQuery(id+"F4.opExtrude","SWEPT_FACE",FACE,{"disambiguationData":[OSD([subQ0])]})]})]})],"blendedInto":[]});}
            var Q7;
            {var subQ0=sQuery(id+"F0.wireOp",EDGE,"E1.top");var subQ1=makeQuery(id+"F11.opExtrude","CAP_EDGE",EDGE,{"disambiguationData":[OSD([sQuery(id+"F9.wireOp",EDGE,"E34")])],"isStart":true});var subQ2=sQuery(id+"F0.wireOp",EDGE,"E4");Q7=makeQuery(id+"F15.opFillet","BLEND_EDGE",EDGE,{"blendedFrom":[makeQuery(id+"F12.opFillet","BLEND_EDGE",EDGE,{"blendedFrom":[subQ1,makeQuery(id+"F4.boolean.opBoolean","MERGE",FACE,{"derivedFrom":[makeQuery(id+"F3.opExtrude","SWEPT_FACE",FACE,{"disambiguationData":[OSD([subQ2])]}),makeQuery(id+"F4.opExtrude","SWEPT_FACE",FACE,{"disambiguationData":[OSD([subQ2])]})]})],"blendedInto":[makeQuery(id+"F4.boolean.opBoolean","MERGE",FACE,{"derivedFrom":[makeQuery(id+"F3.opExtrude","SWEPT_FACE",FACE,{"disambiguationData":[OSD([subQ2])]}),makeQuery(id+"F4.opExtrude","SWEPT_FACE",FACE,{"disambiguationData":[OSD([subQ2])]})]})]}),makeQuery(id+"F12.opFillet","BLEND_EDGE",EDGE,{"blendedFrom":[subQ1,makeQuery(id+"F4.boolean.opBoolean","MERGE",FACE,{"derivedFrom":[makeQuery(id+"F3.opExtrude","SWEPT_FACE",FACE,{"disambiguationData":[OSD([subQ0])]}),makeQuery(id+"F4.opExtrude","SWEPT_FACE",FACE,{"disambiguationData":[OSD([subQ0])]})]})],"blendedInto":[makeQuery(id+"F4.boolean.opBoolean","MERGE",FACE,{"derivedFrom":[makeQuery(id+"F3.opExtrude","SWEPT_FACE",FACE,{"disambiguationData":[OSD([subQ0])]}),makeQuery(id+"F4.opExtrude","SWEPT_FACE",FACE,{"disambiguationData":[OSD([subQ0])]})]})]})],"blendedInto":[]});}
            fillet(context, id + "F16", {"entities" : qUnion([Q0, Q1, Q2, Q3, Q4, Q5, Q6, Q7]), "radius" : 7.62 * mm, "tangentPropagation" : true, "allowEdgeOverflow" : false});
        }
        {
            var Q0;
            Q0=makeQuery(id+"F11.boolean.opBoolean","MERGE",FACE,{"derivedFrom":[makeQuery(id+"F10.boolean.opBoolean","MERGE",FACE,{"derivedFrom":[makeQuery(id+"F3.opExtrude","CAP_FACE",FACE,{"disambiguationData":[OSD([dummyQuery(id+"F1.planeOp",FACE)])],"isStart":false}),makeQuery(id+"F10.opExtrude","SWEPT_FACE",FACE,{"disambiguationData":[OSD([sQuery(id+"F8.wireOp",EDGE,"E31.top")])]}),makeQuery(id+"F10.opExtrude","SWEPT_FACE",FACE,{"disambiguationData":[OSD([sQuery(id+"F8.wireOp",EDGE,"E33.top")])]})]}),makeQuery(id+"F11.opExtrude","SWEPT_FACE",FACE,{"disambiguationData":[OSD([sQuery(id+"F9.wireOp",EDGE,"E36.top")])]}),makeQuery(id+"F11.opExtrude","SWEPT_FACE",FACE,{"disambiguationData":[OSD([sQuery(id+"F9.wireOp",EDGE,"E37.top")])]})]});
            shell(context, id + "F17", {"entities" : qUnion([Q0]), "thickness" : 0.89 * mm});
        }
        {
            var Q0;
            Q0=qCreatedBy(makeId("Front.planeOp"),FACE);
            var sketch = newSketch(context, id + "F18", { "sketchPlane" : qUnion([Q0])});
            skLineSegment(sketch, "E38.bottom", {"start": v(-39.11, 0) * mm, "end": v(39.11, 0) * mm});
            skLineSegment(sketch, "E38.top", {"start": v(-39.11, 29.9) * mm, "end": v(39.11, 29.9) * mm});
            skLineSegment(sketch, "E38.left", {"start": v(-39.11, 0) * mm, "end": v(-39.11, 29.9) * mm});
            skLineSegment(sketch, "E38.right", {"start": v(39.11, 0) * mm, "end": v(39.11, 29.9) * mm});
            skPoint(sketch, "E38.middle", {"position": v(0, 14.95) * mm});
            skSolve(sketch);
        }
        {
            var Q0;
            Q0 = qSketchRegion(id + "F18", true);
            extrude(context, id + "F19", {"entities" : qUnion([Q0]), "operationType" : NewBodyOperationType.REMOVE, "endBound" : BoundingType.SYMMETRIC, "oppositeDirection" : true, "depth" : 76.2 * mm});
        }
        {
            var Q0;
            Q0=makeQuery(id+"F17.opShell","OFFSET_FACE",FACE,{"disambiguationData":[OSD([sQuery(id+"F2.wireOp",EDGE,"E13")])]});
            extrude(context, id + "F20", {"entities" : qUnion([Q0]), "operationType" : NewBodyOperationType.REMOVE, "endBound" : BoundingType.SYMMETRIC, "oppositeDirection" : true, "depth" : 203.2 * mm});
        }
        {
            var Q0;
            Q0=makeQuery(id+"F17.opShell","OFFSET_FACE",FACE,{"disambiguationData":[OSD([sQuery(id+"F2.wireOp",EDGE,"E15")])]});
            extrude(context, id + "F21", {"entities" : qUnion([Q0]), "operationType" : NewBodyOperationType.REMOVE, "endBound" : BoundingType.SYMMETRIC, "oppositeDirection" : true, "depth" : 203.2 * mm});
        }
        {
            var Q0;
            Q0=qCreatedBy(makeId("Front.planeOp"),FACE);
            var sketch = newSketch(context, id + "F22", { "sketchPlane" : qUnion([Q0])});
            skCircle(sketch, "E39", {"center": v(-1.26, -11.3) * mm, "radius": 2.22 * mm});
            skCircle(sketch, "E40", {"center": v(-5.7, -11.3) * mm, "radius": 2.22 * mm});
            skLineSegment(sketch, "E41.bottom", {"start": v(0.97, -11.3) * mm, "end": v(-7.92, -11.3) * mm});
            skLineSegment(sketch, "E41.top", {"start": v(0.97, -17.23) * mm, "end": v(-7.92, -17.23) * mm});
            skLineSegment(sketch, "E41.left", {"start": v(0.97, -11.3) * mm, "end": v(0.97, -17.23) * mm});
            skLineSegment(sketch, "E41.right", {"start": v(-7.92, -11.3) * mm, "end": v(-7.92, -17.23) * mm});
            skSolve(sketch);
        }
        {
            var Q0;
            Q0 = qSketchRegion(id + "F22", true);
            extrude(context, id + "F23", {"entities" : qUnion([Q0]), "operationType" : NewBodyOperationType.REMOVE, "endBound" : BoundingType.THROUGH_ALL, "oppositeDirection" : true, "depth" : 25.4 * mm});
        }
        {
            var Q0;
            Q0=makeQuery(id+"F14.opFillet","BLEND_EDGE",EDGE,{"blendedFrom":[makeQuery(id+"F13.boolean.opBoolean","INTERSECT",EDGE,{"derivedFrom":[makeQuery(id+"F12.opFillet","BLEND_FACE",FACE,{"disambiguationData":[OSD([sQuery(id+"F8.wireOp",EDGE,"E32")])]}),makeQuery(id+"F13.opExtrude","SWEPT_FACE",FACE,{"disambiguationData":[OSD([sQuery(id+"F2.wireOp",EDGE,"E14")])]})]}),makeQuery(id+"F11.boolean.opBoolean","MERGE",FACE,{"derivedFrom":[makeQuery(id+"F10.boolean.opBoolean","MERGE",FACE,{"derivedFrom":[makeQuery(id+"F3.opExtrude","CAP_FACE",FACE,{"disambiguationData":[OSD([dummyQuery(id+"F1.planeOp",FACE)])],"isStart":false}),makeQuery(id+"F10.opExtrude","SWEPT_FACE",FACE,{"disambiguationData":[OSD([sQuery(id+"F8.wireOp",EDGE,"E31.top")])]}),makeQuery(id+"F10.opExtrude","SWEPT_FACE",FACE,{"disambiguationData":[OSD([sQuery(id+"F8.wireOp",EDGE,"E33.top")])]})]}),makeQuery(id+"F11.opExtrude","SWEPT_FACE",FACE,{"disambiguationData":[OSD([sQuery(id+"F9.wireOp",EDGE,"E36.top")])]}),makeQuery(id+"F11.opExtrude","SWEPT_FACE",FACE,{"disambiguationData":[OSD([sQuery(id+"F9.wireOp",EDGE,"E37.top")])]})]})],"blendedInto":[makeQuery(id+"F11.boolean.opBoolean","MERGE",FACE,{"derivedFrom":[makeQuery(id+"F10.boolean.opBoolean","MERGE",FACE,{"derivedFrom":[makeQuery(id+"F3.opExtrude","CAP_FACE",FACE,{"disambiguationData":[OSD([dummyQuery(id+"F1.planeOp",FACE)])],"isStart":false}),makeQuery(id+"F10.opExtrude","SWEPT_FACE",FACE,{"disambiguationData":[OSD([sQuery(id+"F8.wireOp",EDGE,"E31.top")])]}),makeQuery(id+"F10.opExtrude","SWEPT_FACE",FACE,{"disambiguationData":[OSD([sQuery(id+"F8.wireOp",EDGE,"E33.top")])]})]}),makeQuery(id+"F11.opExtrude","SWEPT_FACE",FACE,{"disambiguationData":[OSD([sQuery(id+"F9.wireOp",EDGE,"E36.top")])]}),makeQuery(id+"F11.opExtrude","SWEPT_FACE",FACE,{"disambiguationData":[OSD([sQuery(id+"F9.wireOp",EDGE,"E37.top")])]})]})]});
            var Q1;
            {var subQ0=sQuery(id+"F2.wireOp",EDGE,"E8");Q1=makeQuery(id+"F17.opShell","OFFSET_EDGE",EDGE,{"disambiguationData":[OSD([subQ0]),TDD([makeQuery(id+"F13.boolean.opBoolean","COPY",EDGE,{"disambiguationData":[TD([makeQuery(id+"F12.opFillet","BLEND_FACE",FACE,{"disambiguationData":[OSD([sQuery(id+"F8.wireOp",EDGE,"E32")])]})])],"derivedFrom":makeQuery(id+"F13.opExtrude","CAP_EDGE",EDGE,{"disambiguationData":[OSD([subQ0])],"isStart":true})})])]});}
            var Q2;
            {var subQ0=makeQuery(id+"F11.opExtrude","SWEPT_FACE",FACE,{"disambiguationData":[OSD([sQuery(id+"F9.wireOp",EDGE,"E36.top")])]});var subQ1=makeQuery(id+"F10.opExtrude","SWEPT_FACE",FACE,{"disambiguationData":[OSD([sQuery(id+"F8.wireOp",EDGE,"E33.top")])]});var subQ2=makeQuery(id+"F10.opExtrude","SWEPT_FACE",FACE,{"disambiguationData":[OSD([sQuery(id+"F8.wireOp",EDGE,"E31.top")])]});var subQ3=makeQuery(id+"F3.opExtrude","CAP_FACE",FACE,{"disambiguationData":[OSD([dummyQuery(id+"F1.planeOp",FACE)])],"isStart":false});var subQ5=makeQuery(id+"F11.opExtrude","SWEPT_FACE",FACE,{"disambiguationData":[OSD([sQuery(id+"F9.wireOp",EDGE,"E37.top")])]});var subQ6=sQuery(id+"F2.wireOp",EDGE,"E12");var subQ7=makeQuery(id+"F13.opExtrude","SWEPT_FACE",FACE,{"disambiguationData":[OSD([subQ6])]});var subQ11=makeQuery(id+"F13.boolean.opBoolean","COPY",FACE,{"derivedFrom":subQ7});var subQ27=sQuery(id+"F0.wireOp",EDGE,"E1.bottom");var subQ38=makeQuery(id+"F3.opExtrude","SWEPT_FACE",FACE,{"disambiguationData":[OSD([subQ27])]});var subQ47=sQuery(id+"F0.wireOp",EDGE,"E0.left");Q2=makeQuery(id+"F23.boolean.opBoolean","SPLIT",FACE,{"disambiguationData":[TD([subQ11])],"derivedFrom":makeQuery(id+"F21.boolean.opBoolean","SPLIT",FACE,{"disambiguationData":[TD([subQ38])],"derivedFrom":makeQuery(id+"F20.boolean.opBoolean","SPLIT",FACE,{"disambiguationData":[TD([makeQuery(id+"F3.opExtrude","SWEPT_FACE",FACE,{"disambiguationData":[OSD([subQ47])]})])],"derivedFrom":makeQuery(id+"F11.boolean.opBoolean","MERGE",FACE,{"derivedFrom":[makeQuery(id+"F10.boolean.opBoolean","MERGE",FACE,{"derivedFrom":[subQ3,subQ2,subQ1]}),subQ0,subQ5]})})})});}
            var Q3;
            Q3=makeQuery(id+"F23.boolean.opBoolean","COPY",FACE,{"derivedFrom":makeQuery(id+"F23.opExtrude","SWEPT_FACE",FACE,{"disambiguationData":[OSD([sQuery(id+"F22.wireOp",EDGE,"E40")])]})});
            var Q4;
            Q4=makeQuery(id+"F23.boolean.opBoolean","COPY",FACE,{"derivedFrom":makeQuery(id+"F23.opExtrude","SWEPT_FACE",FACE,{"disambiguationData":[OSD([sQuery(id+"F22.wireOp",EDGE,"E39")])]})});
            var Q5;
            {var subQ4=makeQuery(id+"F11.opExtrude","SWEPT_FACE",FACE,{"disambiguationData":[OSD([sQuery(id+"F9.wireOp",EDGE,"E36.top")])]});var subQ5=makeQuery(id+"F10.opExtrude","SWEPT_FACE",FACE,{"disambiguationData":[OSD([sQuery(id+"F8.wireOp",EDGE,"E33.top")])]});var subQ6=makeQuery(id+"F10.opExtrude","SWEPT_FACE",FACE,{"disambiguationData":[OSD([sQuery(id+"F8.wireOp",EDGE,"E31.top")])]});var subQ7=makeQuery(id+"F3.opExtrude","CAP_FACE",FACE,{"disambiguationData":[OSD([dummyQuery(id+"F1.planeOp",FACE)])],"isStart":false});var subQ8=makeQuery(id+"F11.opExtrude","SWEPT_FACE",FACE,{"disambiguationData":[OSD([sQuery(id+"F9.wireOp",EDGE,"E37.top")])]});var subQ31=sQuery(id+"F0.wireOp",EDGE,"E0.left");var subQ36=makeQuery(id+"F3.opExtrude","SWEPT_FACE",FACE,{"disambiguationData":[OSD([subQ31])]});Q5=makeQuery(id+"F21.boolean.opBoolean","SPLIT",FACE,{"disambiguationData":[TD([subQ36])],"derivedFrom":makeQuery(id+"F20.boolean.opBoolean","SPLIT",FACE,{"disambiguationData":[TD([subQ36])],"derivedFrom":makeQuery(id+"F11.boolean.opBoolean","MERGE",FACE,{"derivedFrom":[makeQuery(id+"F10.boolean.opBoolean","MERGE",FACE,{"derivedFrom":[subQ7,subQ6,subQ5]}),subQ4,subQ8]})})});}
            var Q6;
            {var subQ4=sQuery(id+"F0.wireOp",EDGE,"E1.top");var subQ8=makeQuery(id+"F11.opExtrude","SWEPT_FACE",FACE,{"disambiguationData":[OSD([sQuery(id+"F9.wireOp",EDGE,"E36.top")])]});var subQ9=makeQuery(id+"F10.opExtrude","SWEPT_FACE",FACE,{"disambiguationData":[OSD([sQuery(id+"F8.wireOp",EDGE,"E33.top")])]});var subQ10=makeQuery(id+"F10.opExtrude","SWEPT_FACE",FACE,{"disambiguationData":[OSD([sQuery(id+"F8.wireOp",EDGE,"E31.top")])]});var subQ12=makeQuery(id+"F3.opExtrude","CAP_FACE",FACE,{"disambiguationData":[OSD([dummyQuery(id+"F1.planeOp",FACE)])],"isStart":false});var subQ13=makeQuery(id+"F11.opExtrude","SWEPT_FACE",FACE,{"disambiguationData":[OSD([sQuery(id+"F9.wireOp",EDGE,"E37.top")])]});var subQ36=makeQuery(id+"F3.opExtrude","SWEPT_FACE",FACE,{"disambiguationData":[OSD([subQ4])]});var subQ46=sQuery(id+"F0.wireOp",EDGE,"E0.right");Q6=makeQuery(id+"F21.boolean.opBoolean","SPLIT",FACE,{"disambiguationData":[TD([subQ36])],"derivedFrom":makeQuery(id+"F20.boolean.opBoolean","SPLIT",FACE,{"disambiguationData":[TD([makeQuery(id+"F3.opExtrude","SWEPT_FACE",FACE,{"disambiguationData":[OSD([subQ46])]})])],"derivedFrom":makeQuery(id+"F11.boolean.opBoolean","MERGE",FACE,{"derivedFrom":[makeQuery(id+"F10.boolean.opBoolean","MERGE",FACE,{"derivedFrom":[subQ12,subQ10,subQ9]}),subQ8,subQ13]})})});}
            var Q7;
            {var subQ4=sQuery(id+"F0.wireOp",EDGE,"E0.right");var subQ10=makeQuery(id+"F3.opExtrude","SWEPT_FACE",FACE,{"disambiguationData":[OSD([subQ4])]});var subQ19=makeQuery(id+"F11.opExtrude","SWEPT_FACE",FACE,{"disambiguationData":[OSD([sQuery(id+"F9.wireOp",EDGE,"E36.top")])]});var subQ20=makeQuery(id+"F10.opExtrude","SWEPT_FACE",FACE,{"disambiguationData":[OSD([sQuery(id+"F8.wireOp",EDGE,"E33.top")])]});var subQ21=makeQuery(id+"F10.opExtrude","SWEPT_FACE",FACE,{"disambiguationData":[OSD([sQuery(id+"F8.wireOp",EDGE,"E31.top")])]});var subQ23=makeQuery(id+"F3.opExtrude","CAP_FACE",FACE,{"disambiguationData":[OSD([dummyQuery(id+"F1.planeOp",FACE)])],"isStart":false});var subQ24=makeQuery(id+"F11.opExtrude","SWEPT_FACE",FACE,{"disambiguationData":[OSD([sQuery(id+"F9.wireOp",EDGE,"E37.top")])]});Q7=makeQuery(id+"F21.boolean.opBoolean","SPLIT",FACE,{"disambiguationData":[TD([subQ10])],"derivedFrom":makeQuery(id+"F20.boolean.opBoolean","SPLIT",FACE,{"disambiguationData":[TD([subQ10])],"derivedFrom":makeQuery(id+"F11.boolean.opBoolean","MERGE",FACE,{"derivedFrom":[makeQuery(id+"F10.boolean.opBoolean","MERGE",FACE,{"derivedFrom":[subQ23,subQ21,subQ20]}),subQ19,subQ24]})})});}
            var Q8;
            Q8=makeQuery(id+"F13.boolean.opBoolean","COPY",FACE,{"derivedFrom":makeQuery(id+"F13.opExtrude","SWEPT_FACE",FACE,{"disambiguationData":[OSD([sQuery(id+"F2.wireOp",EDGE,"E21")])]})});
            var Q9;
            Q9=makeQuery(id+"F13.boolean.opBoolean","COPY",FACE,{"derivedFrom":makeQuery(id+"F13.opExtrude","SWEPT_FACE",FACE,{"disambiguationData":[OSD([sQuery(id+"F2.wireOp",EDGE,"E18")])]})});
            var Q10;
            Q10=makeQuery(id+"F13.boolean.opBoolean","COPY",FACE,{"derivedFrom":makeQuery(id+"F13.opExtrude","SWEPT_FACE",FACE,{"disambiguationData":[OSD([sQuery(id+"F2.wireOp",EDGE,"E13")])]})});
            var Q11;
            Q11=makeQuery(id+"F13.boolean.opBoolean","COPY",FACE,{"derivedFrom":makeQuery(id+"F13.opExtrude","SWEPT_FACE",FACE,{"disambiguationData":[OSD([sQuery(id+"F2.wireOp",EDGE,"E15")])]})});
            fillet(context, id + "F24", {"entities" : qUnion([Q0, Q1, Q2, Q3, Q4, Q5, Q6, Q7, Q8, Q9, Q10, Q11]), "radius" : 0.25 * mm, "tangentPropagation" : true, "allowEdgeOverflow" : false});
        }
        {
            var Q0;
            Q0=qCreatedBy(makeId("Top.planeOp"),FACE);
            var sketch = newSketch(context, id + "F25", { "sketchPlane" : qUnion([Q0])});
            skCircle(sketch, "E42", {"center": v(-10.52, 24.94) * mm, "radius": 2.8 * mm});
            skCircle(sketch, "E43", {"center": v(10.52, 24.94) * mm, "radius": 2.8 * mm});
            skCircle(sketch, "E44", {"center": v(24.94, 10.52) * mm, "radius": 2.8 * mm});
            skCircle(sketch, "E45", {"center": v(24.94, -10.52) * mm, "radius": 2.8 * mm});
            skCircle(sketch, "E46", {"center": v(10.52, -24.94) * mm, "radius": 2.8 * mm});
            skCircle(sketch, "E47", {"center": v(-10.52, -24.94) * mm, "radius": 2.8 * mm});
            skCircle(sketch, "E48", {"center": v(-24.94, 10.52) * mm, "radius": 2.8 * mm});
            skCircle(sketch, "E49", {"center": v(-10.52, 24.94) * mm, "radius": 3.68 * mm});
            skCircle(sketch, "E50", {"center": v(10.52, 24.94) * mm, "radius": 3.68 * mm});
            skCircle(sketch, "E51", {"center": v(24.94, 10.52) * mm, "radius": 3.68 * mm});
            skCircle(sketch, "E52", {"center": v(24.94, -10.52) * mm, "radius": 3.68 * mm});
            skCircle(sketch, "E53", {"center": v(10.52, -24.94) * mm, "radius": 3.68 * mm});
            skCircle(sketch, "E54", {"center": v(-10.52, -24.94) * mm, "radius": 3.68 * mm});
            skCircle(sketch, "E55", {"center": v(-24.94, 10.52) * mm, "radius": 3.68 * mm});
            skLineSegment(sketch, "E56.bottom", {"start": v(-6.83, 28.63) * mm, "end": v(-14.2, 28.63) * mm});
            skLineSegment(sketch, "E56.top", {"start": v(-6.83, 21.26) * mm, "end": v(-14.2, 21.26) * mm});
            skLineSegment(sketch, "E56.left", {"start": v(-6.83, 28.63) * mm, "end": v(-6.83, 21.26) * mm});
            skLineSegment(sketch, "E56.right", {"start": v(-14.2, 28.63) * mm, "end": v(-14.2, 21.26) * mm});
            skLineSegment(sketch, "E57.bottom", {"start": v(14.2, 28.63) * mm, "end": v(6.83, 28.63) * mm});
            skLineSegment(sketch, "E57.top", {"start": v(14.2, 21.26) * mm, "end": v(6.83, 21.26) * mm});
            skLineSegment(sketch, "E57.left", {"start": v(14.2, 28.63) * mm, "end": v(14.2, 21.26) * mm});
            skLineSegment(sketch, "E57.right", {"start": v(6.83, 28.63) * mm, "end": v(6.83, 21.26) * mm});
            skLineSegment(sketch, "E58.bottom", {"start": v(28.63, 14.2) * mm, "end": v(21.26, 14.2) * mm});
            skLineSegment(sketch, "E58.top", {"start": v(28.63, 6.83) * mm, "end": v(21.26, 6.83) * mm});
            skLineSegment(sketch, "E58.left", {"start": v(28.63, 14.2) * mm, "end": v(28.63, 6.83) * mm});
            skLineSegment(sketch, "E58.right", {"start": v(21.26, 14.2) * mm, "end": v(21.26, 6.83) * mm});
            skLineSegment(sketch, "E59.bottom", {"start": v(28.63, -6.83) * mm, "end": v(21.26, -6.83) * mm});
            skLineSegment(sketch, "E59.top", {"start": v(28.63, -14.2) * mm, "end": v(21.26, -14.2) * mm});
            skLineSegment(sketch, "E59.left", {"start": v(28.63, -6.83) * mm, "end": v(28.63, -14.2) * mm});
            skLineSegment(sketch, "E59.right", {"start": v(21.26, -6.83) * mm, "end": v(21.26, -14.2) * mm});
            skLineSegment(sketch, "E60.bottom", {"start": v(14.2, -21.26) * mm, "end": v(6.83, -21.26) * mm});
            skLineSegment(sketch, "E60.top", {"start": v(14.2, -28.63) * mm, "end": v(6.83, -28.63) * mm});
            skLineSegment(sketch, "E60.left", {"start": v(14.2, -21.26) * mm, "end": v(14.2, -28.63) * mm});
            skLineSegment(sketch, "E60.right", {"start": v(6.83, -21.26) * mm, "end": v(6.83, -28.63) * mm});
            skLineSegment(sketch, "E61.bottom", {"start": v(-6.83, -21.26) * mm, "end": v(-14.2, -21.26) * mm});
            skLineSegment(sketch, "E61.top", {"start": v(-6.83, -28.63) * mm, "end": v(-14.2, -28.63) * mm});
            skLineSegment(sketch, "E61.left", {"start": v(-6.83, -21.26) * mm, "end": v(-6.83, -28.63) * mm});
            skLineSegment(sketch, "E61.right", {"start": v(-14.2, -21.26) * mm, "end": v(-14.2, -28.63) * mm});
            skLineSegment(sketch, "E62.bottom", {"start": v(-21.26, 14.2) * mm, "end": v(-28.63, 14.2) * mm});
            skLineSegment(sketch, "E62.top", {"start": v(-21.26, 6.83) * mm, "end": v(-28.63, 6.83) * mm});
            skLineSegment(sketch, "E62.left", {"start": v(-21.26, 14.2) * mm, "end": v(-21.26, 6.83) * mm});
            skLineSegment(sketch, "E62.right", {"start": v(-28.63, 14.2) * mm, "end": v(-28.63, 6.83) * mm});
            skLineSegment(sketch, "E63", {"start": v(10.52, -28.63) * mm, "end": v(14.2, -27.36) * mm});
            skLineSegment(sketch, "E64", {"start": v(-10.52, -28.63) * mm, "end": v(-14.2, -27.36) * mm});
            skLineSegment(sketch, "E65", {"start": v(28.63, -10.52) * mm, "end": v(27.36, -14.2) * mm});
            skLineSegment(sketch, "E66", {"start": v(28.63, 10.52) * mm, "end": v(27.36, 14.2) * mm});
            skLineSegment(sketch, "E67", {"start": v(10.52, 28.63) * mm, "end": v(14.2, 27.36) * mm});
            skLineSegment(sketch, "E68", {"start": v(-10.52, 28.63) * mm, "end": v(-14.2, 27.36) * mm});
            skLineSegment(sketch, "E69", {"start": v(-28.63, 10.52) * mm, "end": v(-27.36, 14.2) * mm});
            skCircle(sketch, "E70", {"center": v(-24.94, -10.52) * mm, "radius": 3.68 * mm});
            skCircle(sketch, "E71", {"center": v(-24.94, -10.52) * mm, "radius": 2.8 * mm});
            skLineSegment(sketch, "E72.bottom", {"start": v(-21.26, -6.83) * mm, "end": v(-28.63, -6.83) * mm});
            skLineSegment(sketch, "E72.top", {"start": v(-21.26, -14.2) * mm, "end": v(-28.63, -14.2) * mm});
            skLineSegment(sketch, "E72.left", {"start": v(-21.26, -6.83) * mm, "end": v(-21.26, -14.2) * mm});
            skLineSegment(sketch, "E72.right", {"start": v(-28.63, -6.83) * mm, "end": v(-28.63, -14.2) * mm});
            skLineSegment(sketch, "E73", {"start": v(-28.63, -10.52) * mm, "end": v(-27.36, -14.2) * mm});
            skSolve(sketch);
        }
        {
            var Q0;
            {var subQ0=sQuery(id+"F25.wireOp",EDGE,"E56.bottom");var subQ3=sQuery(id+"F25.wireOp",EDGE,"E56.left");var subQ5=makeQuery(id+"F25.imprint","INTERSECT",VERTEX,{"derivedFrom":[subQ0,subQ3]});Q0=makeQuery(id+"F25.imprint","IMPRINT",FACE,{"disambiguationData":[TD([[makeQuery(id+"F25.imprint","IMPRINT",EDGE,{"disambiguationData":[TD([[subQ5,-1.0]])],"derivedFrom":subQ3}),-1.0]])]});}
            var Q1;
            {var subQ0=sQuery(id+"F25.wireOp",EDGE,"E57.bottom");var subQ3=sQuery(id+"F25.wireOp",EDGE,"E57.right");var subQ5=makeQuery(id+"F25.imprint","INTERSECT",VERTEX,{"derivedFrom":[subQ0,subQ3]});Q1=makeQuery(id+"F25.imprint","IMPRINT",FACE,{"disambiguationData":[TD([[makeQuery(id+"F25.imprint","IMPRINT",EDGE,{"disambiguationData":[TD([[subQ5,-1.0]])],"derivedFrom":subQ3}),1.0]])]});}
            var Q2;
            {var subQ0=sQuery(id+"F25.wireOp",EDGE,"E58.left");var subQ3=sQuery(id+"F25.wireOp",EDGE,"E58.top");var subQ5=makeQuery(id+"F25.imprint","INTERSECT",VERTEX,{"derivedFrom":[subQ3,subQ0]});Q2=makeQuery(id+"F25.imprint","IMPRINT",FACE,{"disambiguationData":[TD([[makeQuery(id+"F25.imprint","IMPRINT",EDGE,{"disambiguationData":[TD([[subQ5,-1.0]])],"derivedFrom":subQ3}),-1.0]])]});}
            var Q3;
            {var subQ0=sQuery(id+"F25.wireOp",EDGE,"E59.left");var subQ3=sQuery(id+"F25.wireOp",EDGE,"E59.bottom");var subQ5=makeQuery(id+"F25.imprint","INTERSECT",VERTEX,{"derivedFrom":[subQ3,subQ0]});Q3=makeQuery(id+"F25.imprint","IMPRINT",FACE,{"disambiguationData":[TD([[makeQuery(id+"F25.imprint","IMPRINT",EDGE,{"disambiguationData":[TD([[subQ5,-1.0]])],"derivedFrom":subQ3}),1.0]])]});}
            var Q4;
            {var subQ0=sQuery(id+"F25.wireOp",EDGE,"E60.top");var subQ3=sQuery(id+"F25.wireOp",EDGE,"E60.right");var subQ5=makeQuery(id+"F25.imprint","INTERSECT",VERTEX,{"derivedFrom":[subQ0,subQ3]});Q4=makeQuery(id+"F25.imprint","IMPRINT",FACE,{"disambiguationData":[TD([[makeQuery(id+"F25.imprint","IMPRINT",EDGE,{"disambiguationData":[TD([[subQ5,1.0]])],"derivedFrom":subQ3}),1.0]])]});}
            var Q5;
            {var subQ0=sQuery(id+"F25.wireOp",EDGE,"E61.top");var subQ3=sQuery(id+"F25.wireOp",EDGE,"E61.left");var subQ5=makeQuery(id+"F25.imprint","INTERSECT",VERTEX,{"derivedFrom":[subQ0,subQ3]});Q5=makeQuery(id+"F25.imprint","IMPRINT",FACE,{"disambiguationData":[TD([[makeQuery(id+"F25.imprint","IMPRINT",EDGE,{"disambiguationData":[TD([[subQ5,1.0]])],"derivedFrom":subQ3}),-1.0]])]});}
            var Q6;
            {var subQ0=sQuery(id+"F25.wireOp",EDGE,"E62.right");var subQ3=sQuery(id+"F25.wireOp",EDGE,"E62.top");var subQ5=makeQuery(id+"F25.imprint","INTERSECT",VERTEX,{"derivedFrom":[subQ3,subQ0]});Q6=makeQuery(id+"F25.imprint","IMPRINT",FACE,{"disambiguationData":[TD([[makeQuery(id+"F25.imprint","IMPRINT",EDGE,{"disambiguationData":[TD([[subQ5,1.0]])],"derivedFrom":subQ3}),-1.0]])]});}
            var Q7;
            {var subQ0=sQuery(id+"F25.wireOp",EDGE,"E68");var subQ1=sQuery(id+"F25.wireOp",EDGE,"E49");var subQ3=makeQuery(id+"F25.imprint","INTERSECT",VERTEX,{"derivedFrom":[subQ1,subQ0]});Q7=makeQuery(id+"F25.imprint","IMPRINT",FACE,{"disambiguationData":[TD([[makeQuery(id+"F25.imprint","IMPRINT",EDGE,{"disambiguationData":[TD([[subQ3,1.0]])],"derivedFrom":subQ1}),1.0]])]});}
            var Q8;
            {var subQ0=sQuery(id+"F25.wireOp",EDGE,"E56.right");var subQ1=sQuery(id+"F25.wireOp",EDGE,"E49");var subQ2=makeQuery(id+"F25.imprint","INTERSECT",VERTEX,{"derivedFrom":[subQ1,subQ0]});Q8=makeQuery(id+"F25.imprint","IMPRINT",FACE,{"disambiguationData":[TD([[makeQuery(id+"F25.imprint","IMPRINT",EDGE,{"disambiguationData":[TD([[subQ2,1.0]])],"derivedFrom":subQ1}),-1.0]])]});}
            var Q9;
            {var subQ0=sQuery(id+"F25.wireOp",EDGE,"E57.left");var subQ1=sQuery(id+"F25.wireOp",EDGE,"E50");var subQ2=makeQuery(id+"F25.imprint","INTERSECT",VERTEX,{"derivedFrom":[subQ1,subQ0]});Q9=makeQuery(id+"F25.imprint","IMPRINT",FACE,{"disambiguationData":[TD([[makeQuery(id+"F25.imprint","IMPRINT",EDGE,{"disambiguationData":[TD([[subQ2,-1.0]])],"derivedFrom":subQ1}),-1.0]])]});}
            var Q10;
            {var subQ0=sQuery(id+"F25.wireOp",EDGE,"E67");var subQ1=sQuery(id+"F25.wireOp",EDGE,"E50");var subQ3=makeQuery(id+"F25.imprint","INTERSECT",VERTEX,{"derivedFrom":[subQ1,subQ0]});Q10=makeQuery(id+"F25.imprint","IMPRINT",FACE,{"disambiguationData":[TD([[makeQuery(id+"F25.imprint","IMPRINT",EDGE,{"disambiguationData":[TD([[subQ3,-1.0]])],"derivedFrom":subQ1}),1.0]])]});}
            var Q11;
            {var subQ0=sQuery(id+"F25.wireOp",EDGE,"E66");var subQ1=sQuery(id+"F25.wireOp",EDGE,"E51");var subQ3=makeQuery(id+"F25.imprint","INTERSECT",VERTEX,{"derivedFrom":[subQ1,subQ0]});Q11=makeQuery(id+"F25.imprint","IMPRINT",FACE,{"disambiguationData":[TD([[makeQuery(id+"F25.imprint","IMPRINT",EDGE,{"disambiguationData":[TD([[subQ3,1.0]])],"derivedFrom":subQ1}),1.0]])]});}
            var Q12;
            {var subQ0=sQuery(id+"F25.wireOp",EDGE,"E58.bottom");var subQ1=sQuery(id+"F25.wireOp",EDGE,"E51");var subQ2=makeQuery(id+"F25.imprint","INTERSECT",VERTEX,{"derivedFrom":[subQ1,subQ0]});Q12=makeQuery(id+"F25.imprint","IMPRINT",FACE,{"disambiguationData":[TD([[makeQuery(id+"F25.imprint","IMPRINT",EDGE,{"disambiguationData":[TD([[subQ2,1.0]])],"derivedFrom":subQ1}),-1.0]])]});}
            var Q13;
            {var subQ0=sQuery(id+"F25.wireOp",EDGE,"E59.top");var subQ1=sQuery(id+"F25.wireOp",EDGE,"E52");var subQ2=makeQuery(id+"F25.imprint","INTERSECT",VERTEX,{"derivedFrom":[subQ1,subQ0]});Q13=makeQuery(id+"F25.imprint","IMPRINT",FACE,{"disambiguationData":[TD([[makeQuery(id+"F25.imprint","IMPRINT",EDGE,{"disambiguationData":[TD([[subQ2,-1.0]])],"derivedFrom":subQ1}),-1.0]])]});}
            var Q14;
            {var subQ0=sQuery(id+"F25.wireOp",EDGE,"E65");var subQ1=sQuery(id+"F25.wireOp",EDGE,"E52");var subQ3=makeQuery(id+"F25.imprint","INTERSECT",VERTEX,{"derivedFrom":[subQ1,subQ0]});Q14=makeQuery(id+"F25.imprint","IMPRINT",FACE,{"disambiguationData":[TD([[makeQuery(id+"F25.imprint","IMPRINT",EDGE,{"disambiguationData":[TD([[subQ3,-1.0]])],"derivedFrom":subQ1}),1.0]])]});}
            var Q15;
            {var subQ0=sQuery(id+"F25.wireOp",EDGE,"E63");var subQ1=sQuery(id+"F25.wireOp",EDGE,"E53");var subQ3=makeQuery(id+"F25.imprint","INTERSECT",VERTEX,{"derivedFrom":[subQ1,subQ0]});Q15=makeQuery(id+"F25.imprint","IMPRINT",FACE,{"disambiguationData":[TD([[makeQuery(id+"F25.imprint","IMPRINT",EDGE,{"disambiguationData":[TD([[subQ3,1.0]])],"derivedFrom":subQ1}),1.0]])]});}
            var Q16;
            {var subQ0=sQuery(id+"F25.wireOp",EDGE,"E60.left");var subQ1=sQuery(id+"F25.wireOp",EDGE,"E53");var subQ2=makeQuery(id+"F25.imprint","INTERSECT",VERTEX,{"derivedFrom":[subQ1,subQ0]});Q16=makeQuery(id+"F25.imprint","IMPRINT",FACE,{"disambiguationData":[TD([[makeQuery(id+"F25.imprint","IMPRINT",EDGE,{"disambiguationData":[TD([[subQ2,1.0]])],"derivedFrom":subQ1}),-1.0]])]});}
            var Q17;
            {var subQ0=sQuery(id+"F25.wireOp",EDGE,"E61.right");var subQ1=sQuery(id+"F25.wireOp",EDGE,"E54");var subQ2=makeQuery(id+"F25.imprint","INTERSECT",VERTEX,{"derivedFrom":[subQ1,subQ0]});Q17=makeQuery(id+"F25.imprint","IMPRINT",FACE,{"disambiguationData":[TD([[makeQuery(id+"F25.imprint","IMPRINT",EDGE,{"disambiguationData":[TD([[subQ2,-1.0]])],"derivedFrom":subQ1}),-1.0]])]});}
            var Q18;
            {var subQ0=sQuery(id+"F25.wireOp",EDGE,"E64");var subQ1=sQuery(id+"F25.wireOp",EDGE,"E54");var subQ3=makeQuery(id+"F25.imprint","INTERSECT",VERTEX,{"derivedFrom":[subQ1,subQ0]});Q18=makeQuery(id+"F25.imprint","IMPRINT",FACE,{"disambiguationData":[TD([[makeQuery(id+"F25.imprint","IMPRINT",EDGE,{"disambiguationData":[TD([[subQ3,-1.0]])],"derivedFrom":subQ1}),1.0]])]});}
            var Q19;
            {var subQ0=sQuery(id+"F25.wireOp",EDGE,"E62.bottom");var subQ1=sQuery(id+"F25.wireOp",EDGE,"E55");var subQ2=makeQuery(id+"F25.imprint","INTERSECT",VERTEX,{"derivedFrom":[subQ1,subQ0]});Q19=makeQuery(id+"F25.imprint","IMPRINT",FACE,{"disambiguationData":[TD([[makeQuery(id+"F25.imprint","IMPRINT",EDGE,{"disambiguationData":[TD([[subQ2,-1.0]])],"derivedFrom":subQ1}),-1.0]])]});}
            var Q20;
            {var subQ0=sQuery(id+"F25.wireOp",EDGE,"E69");var subQ1=sQuery(id+"F25.wireOp",EDGE,"E55");var subQ3=makeQuery(id+"F25.imprint","INTERSECT",VERTEX,{"derivedFrom":[subQ1,subQ0]});Q20=makeQuery(id+"F25.imprint","IMPRINT",FACE,{"disambiguationData":[TD([[makeQuery(id+"F25.imprint","IMPRINT",EDGE,{"disambiguationData":[TD([[subQ3,-1.0]])],"derivedFrom":subQ1}),1.0]])]});}
            var Q21;
            Q21=makeQuery(id+"F25.imprint","IMPRINT",FACE,{"disambiguationData":[TD([[makeQuery(id+"F25.imprint","IMPRINT",EDGE,{"derivedFrom":sQuery(id+"F25.wireOp",EDGE,"E42")}),-1.0]])]});
            var Q22;
            Q22=makeQuery(id+"F25.imprint","IMPRINT",FACE,{"disambiguationData":[TD([[makeQuery(id+"F25.imprint","IMPRINT",EDGE,{"derivedFrom":sQuery(id+"F25.wireOp",EDGE,"E43")}),-1.0]])]});
            var Q23;
            Q23=makeQuery(id+"F25.imprint","IMPRINT",FACE,{"disambiguationData":[TD([[makeQuery(id+"F25.imprint","IMPRINT",EDGE,{"derivedFrom":sQuery(id+"F25.wireOp",EDGE,"E44")}),-1.0]])]});
            var Q24;
            Q24=makeQuery(id+"F25.imprint","IMPRINT",FACE,{"disambiguationData":[TD([[makeQuery(id+"F25.imprint","IMPRINT",EDGE,{"derivedFrom":sQuery(id+"F25.wireOp",EDGE,"E45")}),-1.0]])]});
            var Q25;
            Q25=makeQuery(id+"F25.imprint","IMPRINT",FACE,{"disambiguationData":[TD([[makeQuery(id+"F25.imprint","IMPRINT",EDGE,{"derivedFrom":sQuery(id+"F25.wireOp",EDGE,"E46")}),-1.0]])]});
            var Q26;
            Q26=makeQuery(id+"F25.imprint","IMPRINT",FACE,{"disambiguationData":[TD([[makeQuery(id+"F25.imprint","IMPRINT",EDGE,{"derivedFrom":sQuery(id+"F25.wireOp",EDGE,"E47")}),-1.0]])]});
            var Q27;
            Q27=makeQuery(id+"F25.imprint","IMPRINT",FACE,{"disambiguationData":[TD([[makeQuery(id+"F25.imprint","IMPRINT",EDGE,{"derivedFrom":sQuery(id+"F25.wireOp",EDGE,"E48")}),-1.0]])]});
            var Q28;
            Q28=makeQuery(id+"F25.imprint","IMPRINT",FACE,{"disambiguationData":[TD([[makeQuery(id+"F25.imprint","IMPRINT",EDGE,{"derivedFrom":sQuery(id+"F25.wireOp",EDGE,"E71")}),-1.0]])]});
            var Q29;
            {var subQ0=sQuery(id+"F25.wireOp",EDGE,"E73");var subQ1=sQuery(id+"F25.wireOp",EDGE,"E70");var subQ3=makeQuery(id+"F25.imprint","INTERSECT",VERTEX,{"derivedFrom":[subQ1,subQ0]});Q29=makeQuery(id+"F25.imprint","IMPRINT",FACE,{"disambiguationData":[TD([[makeQuery(id+"F25.imprint","IMPRINT",EDGE,{"disambiguationData":[TD([[subQ3,1.0]])],"derivedFrom":subQ1}),1.0]])]});}
            var Q30;
            {var subQ0=sQuery(id+"F25.wireOp",EDGE,"E72.top");var subQ1=sQuery(id+"F25.wireOp",EDGE,"E70");var subQ2=makeQuery(id+"F25.imprint","INTERSECT",VERTEX,{"derivedFrom":[subQ1,subQ0]});Q30=makeQuery(id+"F25.imprint","IMPRINT",FACE,{"disambiguationData":[TD([[makeQuery(id+"F25.imprint","IMPRINT",EDGE,{"disambiguationData":[TD([[subQ2,1.0]])],"derivedFrom":subQ1}),-1.0]])]});}
            var Q31;
            {var subQ0=sQuery(id+"F25.wireOp",EDGE,"E72.right");var subQ3=sQuery(id+"F25.wireOp",EDGE,"E72.bottom");var subQ5=makeQuery(id+"F25.imprint","INTERSECT",VERTEX,{"derivedFrom":[subQ3,subQ0]});Q31=makeQuery(id+"F25.imprint","IMPRINT",FACE,{"disambiguationData":[TD([[makeQuery(id+"F25.imprint","IMPRINT",EDGE,{"disambiguationData":[TD([[subQ5,1.0]])],"derivedFrom":subQ3}),1.0]])]});}
            extrude(context, id + "F26", {"entities" : qUnion([Q0, Q1, Q2, Q3, Q4, Q5, Q6, Q7, Q8, Q9, Q10, Q11, Q12, Q13, Q14, Q15, Q16, Q17, Q18, Q19, Q20, Q21, Q22, Q23, Q24, Q25, Q26, Q27, Q28, Q29, Q30, Q31]), "operationType" : NewBodyOperationType.ADD, "oppositeDirection" : true, "depth" : 3.17 * mm});
        }
        {
            var Q0;
            Q0=makeQuery(id+"F26.opExtrude","CAP_FACE",FACE,{"disambiguationData":[OSD([sQuery(id+"F25.wireOp",EDGE,"E45"),sQuery(id+"F25.wireOp",EDGE,"E52"),sQuery(id+"F25.wireOp",EDGE,"E59.bottom"),sQuery(id+"F25.wireOp",EDGE,"E59.top"),sQuery(id+"F25.wireOp",EDGE,"E59.left"),sQuery(id+"F25.wireOp",EDGE,"E65")])],"isStart":false});
            var sketch = newSketch(context, id + "F27", { "sketchPlane" : qUnion([Q0])});
            skLineSegment(sketch, "E74.bottom", {"start": v(26.38, -14.2) * mm, "end": v(29.2, -14.2) * mm});
            skLineSegment(sketch, "E74.top", {"start": v(26.38, -10.37) * mm, "end": v(29.2, -10.37) * mm});
            skLineSegment(sketch, "E74.left", {"start": v(26.38, -14.2) * mm, "end": v(26.38, -10.37) * mm});
            skLineSegment(sketch, "E74.right", {"start": v(29.2, -14.2) * mm, "end": v(29.2, -10.37) * mm});
            skLineSegment(sketch, "E75.bottom", {"start": v(14.2, 26.76) * mm, "end": v(9.92, 26.76) * mm});
            skLineSegment(sketch, "E75.top", {"start": v(14.2, 28.62) * mm, "end": v(9.92, 28.62) * mm});
            skLineSegment(sketch, "E75.left", {"start": v(14.2, 26.76) * mm, "end": v(14.2, 28.62) * mm});
            skLineSegment(sketch, "E75.right", {"start": v(9.92, 26.76) * mm, "end": v(9.92, 28.62) * mm});
            skLineSegment(sketch, "E76.bottom", {"start": v(14.2, -24.5) * mm, "end": v(9.2, -24.5) * mm});
            skLineSegment(sketch, "E76.top", {"start": v(14.2, -29.18) * mm, "end": v(9.2, -29.18) * mm});
            skLineSegment(sketch, "E76.left", {"start": v(14.2, -24.5) * mm, "end": v(14.2, -29.18) * mm});
            skLineSegment(sketch, "E76.right", {"start": v(9.2, -24.5) * mm, "end": v(9.2, -29.18) * mm});
            skLineSegment(sketch, "E77.bottom", {"start": v(-14.2, -25.57) * mm, "end": v(-9.89, -25.57) * mm});
            skLineSegment(sketch, "E77.top", {"start": v(-14.2, -30.13) * mm, "end": v(-9.89, -30.13) * mm});
            skLineSegment(sketch, "E77.left", {"start": v(-14.2, -25.57) * mm, "end": v(-14.2, -30.13) * mm});
            skLineSegment(sketch, "E77.right", {"start": v(-9.89, -25.57) * mm, "end": v(-9.89, -30.13) * mm});
            skLineSegment(sketch, "E78.bottom", {"start": v(-25.49, -6.83) * mm, "end": v(-28.78, -6.83) * mm});
            skLineSegment(sketch, "E78.top", {"start": v(-25.49, -14.2) * mm, "end": v(-28.78, -14.2) * mm});
            skLineSegment(sketch, "E78.left", {"start": v(-25.49, -6.83) * mm, "end": v(-25.49, -14.2) * mm});
            skLineSegment(sketch, "E78.right", {"start": v(-28.78, -6.83) * mm, "end": v(-28.78, -14.2) * mm});
            skLineSegment(sketch, "E79.bottom", {"start": v(-14.2, 28.71) * mm, "end": v(-10.26, 28.71) * mm});
            skLineSegment(sketch, "E79.top", {"start": v(-14.2, 25.52) * mm, "end": v(-10.26, 25.52) * mm});
            skLineSegment(sketch, "E79.left", {"start": v(-14.2, 28.71) * mm, "end": v(-14.2, 25.52) * mm});
            skLineSegment(sketch, "E79.right", {"start": v(-10.26, 28.71) * mm, "end": v(-10.26, 25.52) * mm});
            skLineSegment(sketch, "E80.bottom", {"start": v(26.4, 14.2) * mm, "end": v(30.23, 14.2) * mm});
            skLineSegment(sketch, "E80.top", {"start": v(26.4, 10.23) * mm, "end": v(30.23, 10.23) * mm});
            skLineSegment(sketch, "E80.left", {"start": v(26.4, 14.2) * mm, "end": v(26.4, 10.23) * mm});
            skLineSegment(sketch, "E80.right", {"start": v(30.23, 14.2) * mm, "end": v(30.23, 10.23) * mm});
            skCircle(sketch, "E81", {"center": v(-24.94, -10.52) * mm, "radius": 2.8 * mm});
            skPoint(sketch, "E81.centerSnap0", {"position": v(-25.49, -10.52) * mm});
            skCircle(sketch, "E82", {"center": v(-10.52, -24.94) * mm, "radius": 2.8 * mm});
            skCircle(sketch, "E83", {"center": v(10.52, -24.94) * mm, "radius": 2.8 * mm});
            skCircle(sketch, "E84", {"center": v(24.94, -10.52) * mm, "radius": 2.8 * mm});
            skCircle(sketch, "E85", {"center": v(24.94, 10.52) * mm, "radius": 2.8 * mm});
            skCircle(sketch, "E86", {"center": v(10.52, 24.94) * mm, "radius": 2.8 * mm});
            skCircle(sketch, "E87", {"center": v(-10.52, 24.94) * mm, "radius": 2.8 * mm});
            skLineSegment(sketch, "E88.bottom", {"start": v(-24.2, 14.2) * mm, "end": v(-29.54, 14.2) * mm});
            skLineSegment(sketch, "E88.top", {"start": v(-24.2, 9.1) * mm, "end": v(-29.54, 9.1) * mm});
            skLineSegment(sketch, "E88.left", {"start": v(-24.2, 14.2) * mm, "end": v(-24.2, 9.1) * mm});
            skLineSegment(sketch, "E88.right", {"start": v(-29.54, 14.2) * mm, "end": v(-29.54, 9.1) * mm});
            skCircle(sketch, "E89", {"center": v(-24.94, 10.52) * mm, "radius": 2.8 * mm});
            skSolve(sketch);
        }
        {
            var Q0;
            Q0 = qSketchRegion(id + "F27", true);
            var Q1;
            Q1=makeQuery(id+"F3.opExtrude","SWEPT_BODY",BODY,{"disambiguationData":[OSD([sQuery(id+"F0.wireOp",EDGE,"E0.left"),sQuery(id+"F0.wireOp",EDGE,"E0.right"),sQuery(id+"F0.wireOp",EDGE,"E1.bottom"),sQuery(id+"F0.wireOp",EDGE,"E1.top"),sQuery(id+"F0.wireOp",EDGE,"E2"),sQuery(id+"F0.wireOp",EDGE,"E3"),sQuery(id+"F0.wireOp",EDGE,"E4"),sQuery(id+"F0.wireOp",EDGE,"E5")])]});
            extrude(context, id + "F28", {"entities" : qUnion([Q0]), "operationType" : NewBodyOperationType.ADD, "endBound" : BoundingType.UP_TO_BODY, "oppositeDirection" : true, "endBoundEntityBody" : qUnion([Q1]), "depth" : 25.4 * mm});
        }
        {
            var Q0;
            Q0=qCreatedBy(makeId("Right.planeOp"),FACE);
            var sketch = newSketch(context, id + "F29", { "sketchPlane" : qUnion([Q0])});
            skLineSegment(sketch, "E90.bottom", {"start": v(-11.43, -6.02) * mm, "end": v(-3.81, -6.02) * mm});
            skLineSegment(sketch, "E90.top", {"start": v(-12.95, 3.77) * mm, "end": v(-2.29, 3.77) * mm});
            skLineSegment(sketch, "E90.left", {"start": v(-12.95, -4.5) * mm, "end": v(-12.95, 3.77) * mm});
            skLineSegment(sketch, "E90.right", {"start": v(-2.29, -4.5) * mm, "end": v(-2.29, 3.77) * mm});
            skPoint(sketch, "E90.middle", {"position": v(-7.62, -1.12) * mm});
            skPoint(sketch, "E91.visualSharp", {"position": v(-12.95, -6.02) * mm});
            skArc(sketch, "E91.filletArc", {"start": v(-12.95, -4.5) * mm, "mid": v(-12.5, -5.57) * mm, "end": v(-11.43, -6.02) * mm});
            skPoint(sketch, "E92.visualSharp", {"position": v(-2.29, -6.02) * mm});
            skArc(sketch, "E92.filletArc", {"start": v(-3.81, -6.02) * mm, "mid": v(-2.73, -5.57) * mm, "end": v(-2.29, -4.5) * mm});
            skSolve(sketch);
        }
        {
            var Q0;
            Q0 = qSketchRegion(id + "F29", true);
            extrude(context, id + "F30", {"entities" : qUnion([Q0]), "operationType" : NewBodyOperationType.REMOVE, "endBound" : BoundingType.THROUGH_ALL, "oppositeDirection" : true, "depth" : 25.4 * mm});
        }
        {
            var Q0;
            Q0=makeQuery(id+"F26.boolean.opBoolean","INTERSECT",EDGE,{"derivedFrom":[makeQuery(id+"F17.opShell","OFFSET_FACE",FACE,{"disambiguationData":[OSD([sQuery(id+"F0.wireOp",EDGE,"E1.bottom")])]}),makeQuery(id+"F26.opExtrude","SWEPT_FACE",FACE,{"disambiguationData":[OSD([sQuery(id+"F25.wireOp",EDGE,"E57.right")])]})]});
            var Q1;
            {var subQ0=sQuery(id+"F25.wireOp",EDGE,"E57.right");Q1=makeQuery(id+"F32.opFillet","TWEAK_EDGE",EDGE,{"derivedFrom":[makeQuery(id+"F26.boolean.opBoolean","INTERSECT",VERTEX,{"derivedFrom":[makeQuery(id+"F17.opShell","OFFSET_FACE",FACE,{"disambiguationData":[OSD([sQuery(id+"F0.wireOp",EDGE,"E1.bottom")])]}),makeQuery(id+"F26.opExtrude","CAP_FACE",FACE,{"disambiguationData":[OSD([sQuery(id+"F25.wireOp",EDGE,"E43"),sQuery(id+"F25.wireOp",EDGE,"E50"),sQuery(id+"F25.wireOp",EDGE,"E57.bottom"),sQuery(id+"F25.wireOp",EDGE,"E57.left"),subQ0,sQuery(id+"F25.wireOp",EDGE,"E67")])],"isStart":false}),makeQuery(id+"F26.opExtrude","SWEPT_FACE",FACE,{"disambiguationData":[OSD([subQ0])]})]})]});}
            var Q2;
            Q2=makeQuery(id+"F26.boolean.opBoolean","INTERSECT",EDGE,{"derivedFrom":[makeQuery(id+"F17.opShell","OFFSET_FACE",FACE,{"disambiguationData":[OSD([sQuery(id+"F0.wireOp",EDGE,"E1.bottom")])]}),makeQuery(id+"F26.opExtrude","SWEPT_FACE",FACE,{"disambiguationData":[OSD([sQuery(id+"F25.wireOp",EDGE,"E56.left")])]})]});
            var Q3;
            Q3=makeQuery(id+"F26.boolean.opBoolean","INTERSECT",EDGE,{"derivedFrom":[makeQuery(id+"F17.opShell","OFFSET_FACE",FACE,{"disambiguationData":[OSD([sQuery(id+"F0.wireOp",EDGE,"E0.right")])]}),makeQuery(id+"F26.opExtrude","SWEPT_FACE",FACE,{"disambiguationData":[OSD([sQuery(id+"F25.wireOp",EDGE,"E62.top")])]})]});
            var Q4;
            Q4=makeQuery(id+"F26.boolean.opBoolean","INTERSECT",EDGE,{"derivedFrom":[makeQuery(id+"F17.opShell","OFFSET_FACE",FACE,{"disambiguationData":[OSD([sQuery(id+"F0.wireOp",EDGE,"E1.top")])]}),makeQuery(id+"F26.opExtrude","SWEPT_FACE",FACE,{"disambiguationData":[OSD([sQuery(id+"F25.wireOp",EDGE,"E61.left")])]})]});
            var Q5;
            Q5=makeQuery(id+"F26.boolean.opBoolean","INTERSECT",EDGE,{"derivedFrom":[makeQuery(id+"F17.opShell","OFFSET_FACE",FACE,{"disambiguationData":[OSD([sQuery(id+"F0.wireOp",EDGE,"E1.top")])]}),makeQuery(id+"F26.opExtrude","SWEPT_FACE",FACE,{"disambiguationData":[OSD([sQuery(id+"F25.wireOp",EDGE,"E60.right")])]})]});
            var Q6;
            Q6=makeQuery(id+"F26.boolean.opBoolean","INTERSECT",EDGE,{"derivedFrom":[makeQuery(id+"F17.opShell","OFFSET_FACE",FACE,{"disambiguationData":[OSD([sQuery(id+"F0.wireOp",EDGE,"E0.left")])]}),makeQuery(id+"F26.opExtrude","SWEPT_FACE",FACE,{"disambiguationData":[OSD([sQuery(id+"F25.wireOp",EDGE,"E59.bottom")])]})]});
            var Q7;
            Q7=makeQuery(id+"F26.boolean.opBoolean","INTERSECT",EDGE,{"derivedFrom":[makeQuery(id+"F17.opShell","OFFSET_FACE",FACE,{"disambiguationData":[OSD([sQuery(id+"F0.wireOp",EDGE,"E0.left")])]}),makeQuery(id+"F26.opExtrude","SWEPT_FACE",FACE,{"disambiguationData":[OSD([sQuery(id+"F25.wireOp",EDGE,"E58.top")])]})]});
            fillet(context, id + "F31", {"entities" : qUnion([Q0, Q1, Q2, Q3, Q4, Q5, Q6, Q7]), "radius" : 2.03 * mm, "tangentPropagation" : true, "allowEdgeOverflow" : false});
        }
        {
            var Q0;
            {var subQ0=sQuery(id+"F0.wireOp",EDGE,"E1.bottom");var subQ1=sQuery(id+"F0.wireOp",EDGE,"E2");var subQ2=sQuery(id+"F9.wireOp",EDGE,"E35");Q0=makeQuery(id+"F28.boolean.opBoolean","INTERSECT",EDGE,{"derivedFrom":[makeQuery(id+"F17.opShell","OFFSET_FACE",FACE,{"disambiguationData":[OSD([subQ0,subQ1,subQ2]),TDD([makeQuery(id+"F16.opFillet","BLEND_FACE",FACE,{"disambiguationData":[OSD([subQ0,subQ1,subQ2]),TDD([makeQuery(id+"F15.opFillet","BLEND_EDGE",EDGE,{"blendedFrom":[makeQuery(id+"F12.opFillet","BLEND_EDGE",EDGE,{"blendedFrom":[makeQuery(id+"F11.opExtrude","CAP_EDGE",EDGE,{"disambiguationData":[OSD([subQ2])],"isStart":false}),makeQuery(id+"F4.boolean.opBoolean","MERGE",FACE,{"derivedFrom":[makeQuery(id+"F3.opExtrude","SWEPT_FACE",FACE,{"disambiguationData":[OSD([subQ1])]}),makeQuery(id+"F4.opExtrude","SWEPT_FACE",FACE,{"disambiguationData":[OSD([subQ1])]})]})],"blendedInto":[makeQuery(id+"F4.boolean.opBoolean","MERGE",FACE,{"derivedFrom":[makeQuery(id+"F3.opExtrude","SWEPT_FACE",FACE,{"disambiguationData":[OSD([subQ1])]}),makeQuery(id+"F4.opExtrude","SWEPT_FACE",FACE,{"disambiguationData":[OSD([subQ1])]})]})]}),makeQuery(id+"F4.boolean.opBoolean","MERGE",FACE,{"derivedFrom":[makeQuery(id+"F3.opExtrude","SWEPT_FACE",FACE,{"disambiguationData":[OSD([subQ0])]}),makeQuery(id+"F4.opExtrude","SWEPT_FACE",FACE,{"disambiguationData":[OSD([subQ0])]})]})],"blendedInto":[makeQuery(id+"F4.boolean.opBoolean","MERGE",FACE,{"derivedFrom":[makeQuery(id+"F3.opExtrude","SWEPT_FACE",FACE,{"disambiguationData":[OSD([subQ0])]}),makeQuery(id+"F4.opExtrude","SWEPT_FACE",FACE,{"disambiguationData":[OSD([subQ0])]})]})]})]),OD(0.0)]})])]}),makeQuery(id+"F28.opExtrude","CAP_FACE",FACE,{"disambiguationData":[OSD([sQuery(id+"F27.wireOp",EDGE,"E77.bottom"),sQuery(id+"F27.wireOp",EDGE,"E77.top"),sQuery(id+"F27.wireOp",EDGE,"E77.left"),sQuery(id+"F27.wireOp",EDGE,"E77.right"),sQuery(id+"F27.wireOp",EDGE,"E82")])],"isStart":true})]});}
            var Q1;
            Q1=makeQuery(id+"F26.boolean.opBoolean","INTERSECT",EDGE,{"derivedFrom":[makeQuery(id+"F17.opShell","OFFSET_FACE",FACE,{"disambiguationData":[OSD([sQuery(id+"F0.wireOp",EDGE,"E1.bottom"),sQuery(id+"F2.wireOp",EDGE,"E8"),sQuery(id+"F8.wireOp",EDGE,"E32")])]}),makeQuery(id+"F26.opExtrude","CAP_FACE",FACE,{"disambiguationData":[OSD([sQuery(id+"F25.wireOp",EDGE,"E43"),sQuery(id+"F25.wireOp",EDGE,"E50"),sQuery(id+"F25.wireOp",EDGE,"E57.bottom"),sQuery(id+"F25.wireOp",EDGE,"E57.left"),sQuery(id+"F25.wireOp",EDGE,"E57.right"),sQuery(id+"F25.wireOp",EDGE,"E67")])],"isStart":false})]});
            var Q2;
            {var subQ0=sQuery(id+"F0.wireOp",EDGE,"E0.right");var subQ1=sQuery(id+"F9.wireOp",EDGE,"E35");var subQ2=makeQuery(id+"F11.opExtrude","CAP_EDGE",EDGE,{"disambiguationData":[OSD([subQ1])],"isStart":true});var subQ3=sQuery(id+"F0.wireOp",EDGE,"E2");Q2=makeQuery(id+"F28.boolean.opBoolean","INTERSECT",EDGE,{"derivedFrom":[makeQuery(id+"F17.opShell","OFFSET_FACE",FACE,{"disambiguationData":[OSD([subQ0,subQ3,subQ1]),TDD([makeQuery(id+"F16.opFillet","BLEND_FACE",FACE,{"disambiguationData":[OSD([subQ0,subQ3,subQ1]),TDD([makeQuery(id+"F15.opFillet","BLEND_EDGE",EDGE,{"blendedFrom":[makeQuery(id+"F12.opFillet","BLEND_EDGE",EDGE,{"blendedFrom":[subQ2,makeQuery(id+"F4.boolean.opBoolean","MERGE",FACE,{"derivedFrom":[makeQuery(id+"F3.opExtrude","SWEPT_FACE",FACE,{"disambiguationData":[OSD([subQ3])]}),makeQuery(id+"F4.opExtrude","SWEPT_FACE",FACE,{"disambiguationData":[OSD([subQ3])]})]})],"blendedInto":[makeQuery(id+"F4.boolean.opBoolean","MERGE",FACE,{"derivedFrom":[makeQuery(id+"F3.opExtrude","SWEPT_FACE",FACE,{"disambiguationData":[OSD([subQ3])]}),makeQuery(id+"F4.opExtrude","SWEPT_FACE",FACE,{"disambiguationData":[OSD([subQ3])]})]})]}),makeQuery(id+"F12.opFillet","BLEND_EDGE",EDGE,{"blendedFrom":[subQ2,makeQuery(id+"F4.boolean.opBoolean","MERGE",FACE,{"derivedFrom":[makeQuery(id+"F3.opExtrude","SWEPT_FACE",FACE,{"disambiguationData":[OSD([subQ0])]}),makeQuery(id+"F4.opExtrude","SWEPT_FACE",FACE,{"disambiguationData":[OSD([subQ0])]})]})],"blendedInto":[makeQuery(id+"F4.boolean.opBoolean","MERGE",FACE,{"derivedFrom":[makeQuery(id+"F3.opExtrude","SWEPT_FACE",FACE,{"disambiguationData":[OSD([subQ0])]}),makeQuery(id+"F4.opExtrude","SWEPT_FACE",FACE,{"disambiguationData":[OSD([subQ0])]})]})]})],"blendedInto":[]})]),OD(0.0)]})])]}),makeQuery(id+"F28.opExtrude","CAP_FACE",FACE,{"disambiguationData":[OSD([sQuery(id+"F27.wireOp",EDGE,"E78.bottom"),sQuery(id+"F27.wireOp",EDGE,"E78.top"),sQuery(id+"F27.wireOp",EDGE,"E78.left"),sQuery(id+"F27.wireOp",EDGE,"E78.right"),sQuery(id+"F27.wireOp",EDGE,"E81")])],"isStart":true})]});}
            var Q3;
            Q3=makeQuery(id+"F26.boolean.opBoolean","INTERSECT",EDGE,{"derivedFrom":[makeQuery(id+"F17.opShell","OFFSET_FACE",FACE,{"disambiguationData":[OSD([sQuery(id+"F0.wireOp",EDGE,"E1.top"),sQuery(id+"F2.wireOp",EDGE,"E10"),sQuery(id+"F8.wireOp",EDGE,"E30")])]}),makeQuery(id+"F26.opExtrude","CAP_FACE",FACE,{"disambiguationData":[OSD([sQuery(id+"F25.wireOp",EDGE,"E47"),sQuery(id+"F25.wireOp",EDGE,"E54"),sQuery(id+"F25.wireOp",EDGE,"E61.top"),sQuery(id+"F25.wireOp",EDGE,"E61.left"),sQuery(id+"F25.wireOp",EDGE,"E61.right"),sQuery(id+"F25.wireOp",EDGE,"E64")])],"isStart":false})]});
            var Q4;
            Q4=makeQuery(id+"F26.boolean.opBoolean","INTERSECT",EDGE,{"derivedFrom":[makeQuery(id+"F17.opShell","OFFSET_FACE",FACE,{"disambiguationData":[OSD([sQuery(id+"F0.wireOp",EDGE,"E1.top"),sQuery(id+"F2.wireOp",EDGE,"E10"),sQuery(id+"F9.wireOp",EDGE,"E34")])]}),makeQuery(id+"F26.opExtrude","CAP_FACE",FACE,{"disambiguationData":[OSD([sQuery(id+"F25.wireOp",EDGE,"E46"),sQuery(id+"F25.wireOp",EDGE,"E53"),sQuery(id+"F25.wireOp",EDGE,"E60.top"),sQuery(id+"F25.wireOp",EDGE,"E60.left"),sQuery(id+"F25.wireOp",EDGE,"E60.right"),sQuery(id+"F25.wireOp",EDGE,"E63")])],"isStart":false})]});
            var Q5;
            Q5=makeQuery(id+"F26.boolean.opBoolean","INTERSECT",EDGE,{"derivedFrom":[makeQuery(id+"F17.opShell","OFFSET_FACE",FACE,{"disambiguationData":[OSD([sQuery(id+"F0.wireOp",EDGE,"E0.left"),sQuery(id+"F2.wireOp",EDGE,"E9"),sQuery(id+"F9.wireOp",EDGE,"E34")])]}),makeQuery(id+"F26.opExtrude","CAP_FACE",FACE,{"disambiguationData":[OSD([sQuery(id+"F25.wireOp",EDGE,"E45"),sQuery(id+"F25.wireOp",EDGE,"E52"),sQuery(id+"F25.wireOp",EDGE,"E59.bottom"),sQuery(id+"F25.wireOp",EDGE,"E59.top"),sQuery(id+"F25.wireOp",EDGE,"E59.left"),sQuery(id+"F25.wireOp",EDGE,"E65")])],"isStart":false})]});
            var Q6;
            Q6=makeQuery(id+"F26.boolean.opBoolean","INTERSECT",EDGE,{"derivedFrom":[makeQuery(id+"F17.opShell","OFFSET_FACE",FACE,{"disambiguationData":[OSD([sQuery(id+"F0.wireOp",EDGE,"E0.left"),sQuery(id+"F2.wireOp",EDGE,"E9"),sQuery(id+"F8.wireOp",EDGE,"E32")])]}),makeQuery(id+"F26.opExtrude","CAP_FACE",FACE,{"disambiguationData":[OSD([sQuery(id+"F25.wireOp",EDGE,"E44"),sQuery(id+"F25.wireOp",EDGE,"E51"),sQuery(id+"F25.wireOp",EDGE,"E58.bottom"),sQuery(id+"F25.wireOp",EDGE,"E58.top"),sQuery(id+"F25.wireOp",EDGE,"E58.left"),sQuery(id+"F25.wireOp",EDGE,"E66")])],"isStart":false})]});
            var Q7;
            {var subQ0=sQuery(id+"F0.wireOp",EDGE,"E0.right");var subQ1=sQuery(id+"F0.wireOp",EDGE,"E5");var subQ2=sQuery(id+"F8.wireOp",EDGE,"E30");Q7=makeQuery(id+"F28.boolean.opBoolean","INTERSECT",EDGE,{"derivedFrom":[makeQuery(id+"F17.opShell","OFFSET_FACE",FACE,{"disambiguationData":[OSD([subQ0,subQ1,subQ2]),TDD([makeQuery(id+"F16.opFillet","BLEND_FACE",FACE,{"disambiguationData":[OSD([subQ0,subQ1,subQ2]),TDD([makeQuery(id+"F15.opFillet","BLEND_EDGE",EDGE,{"blendedFrom":[makeQuery(id+"F12.opFillet","BLEND_EDGE",EDGE,{"blendedFrom":[makeQuery(id+"F10.opExtrude","CAP_EDGE",EDGE,{"disambiguationData":[OSD([subQ2])],"isStart":false}),makeQuery(id+"F4.boolean.opBoolean","MERGE",FACE,{"derivedFrom":[makeQuery(id+"F3.opExtrude","SWEPT_FACE",FACE,{"disambiguationData":[OSD([subQ1])]}),makeQuery(id+"F4.opExtrude","SWEPT_FACE",FACE,{"disambiguationData":[OSD([subQ1])]})]})],"blendedInto":[makeQuery(id+"F4.boolean.opBoolean","MERGE",FACE,{"derivedFrom":[makeQuery(id+"F3.opExtrude","SWEPT_FACE",FACE,{"disambiguationData":[OSD([subQ1])]}),makeQuery(id+"F4.opExtrude","SWEPT_FACE",FACE,{"disambiguationData":[OSD([subQ1])]})]})]}),makeQuery(id+"F4.boolean.opBoolean","MERGE",FACE,{"derivedFrom":[makeQuery(id+"F3.opExtrude","SWEPT_FACE",FACE,{"disambiguationData":[OSD([subQ0])]}),makeQuery(id+"F4.opExtrude","SWEPT_FACE",FACE,{"disambiguationData":[OSD([subQ0])]})]})],"blendedInto":[makeQuery(id+"F4.boolean.opBoolean","MERGE",FACE,{"derivedFrom":[makeQuery(id+"F3.opExtrude","SWEPT_FACE",FACE,{"disambiguationData":[OSD([subQ0])]}),makeQuery(id+"F4.opExtrude","SWEPT_FACE",FACE,{"disambiguationData":[OSD([subQ0])]})]})]})]),OD(0.0)]})])]}),makeQuery(id+"F28.opExtrude","CAP_FACE",FACE,{"disambiguationData":[OSD([sQuery(id+"F27.wireOp",EDGE,"E88.bottom"),sQuery(id+"F27.wireOp",EDGE,"E88.top"),sQuery(id+"F27.wireOp",EDGE,"E88.left"),sQuery(id+"F27.wireOp",EDGE,"E88.right"),sQuery(id+"F27.wireOp",EDGE,"E89")])],"isStart":true})]});}
            fillet(context, id + "F32", {"entities" : qUnion([Q0, Q1, Q2, Q3, Q4, Q5, Q6, Q7]), "radius" : 0.76 * mm, "tangentPropagation" : true, "allowEdgeOverflow" : false});
        }
        {
            var Q0;
            {var subQ0=sQuery(id+"F0.wireOp",EDGE,"E1.top");var subQ1=sQuery(id+"F8.wireOp",EDGE,"E30");var subQ2=makeQuery(id+"F10.opExtrude","CAP_EDGE",EDGE,{"disambiguationData":[OSD([subQ1])],"isStart":true});var subQ3=sQuery(id+"F0.wireOp",EDGE,"E5");Q0=makeQuery(id+"F28.boolean.opBoolean","INTERSECT",EDGE,{"derivedFrom":[makeQuery(id+"F17.opShell","OFFSET_FACE",FACE,{"disambiguationData":[OSD([subQ0,subQ3,subQ1]),TDD([makeQuery(id+"F16.opFillet","BLEND_FACE",FACE,{"disambiguationData":[OSD([subQ0,subQ3,subQ1]),TDD([makeQuery(id+"F15.opFillet","BLEND_EDGE",EDGE,{"blendedFrom":[makeQuery(id+"F12.opFillet","BLEND_EDGE",EDGE,{"blendedFrom":[subQ2,makeQuery(id+"F4.boolean.opBoolean","MERGE",FACE,{"derivedFrom":[makeQuery(id+"F3.opExtrude","SWEPT_FACE",FACE,{"disambiguationData":[OSD([subQ3])]}),makeQuery(id+"F4.opExtrude","SWEPT_FACE",FACE,{"disambiguationData":[OSD([subQ3])]})]})],"blendedInto":[makeQuery(id+"F4.boolean.opBoolean","MERGE",FACE,{"derivedFrom":[makeQuery(id+"F3.opExtrude","SWEPT_FACE",FACE,{"disambiguationData":[OSD([subQ3])]}),makeQuery(id+"F4.opExtrude","SWEPT_FACE",FACE,{"disambiguationData":[OSD([subQ3])]})]})]}),makeQuery(id+"F12.opFillet","BLEND_EDGE",EDGE,{"blendedFrom":[subQ2,makeQuery(id+"F4.boolean.opBoolean","MERGE",FACE,{"derivedFrom":[makeQuery(id+"F3.opExtrude","SWEPT_FACE",FACE,{"disambiguationData":[OSD([subQ0])]}),makeQuery(id+"F4.opExtrude","SWEPT_FACE",FACE,{"disambiguationData":[OSD([subQ0])]})]})],"blendedInto":[makeQuery(id+"F4.boolean.opBoolean","MERGE",FACE,{"derivedFrom":[makeQuery(id+"F3.opExtrude","SWEPT_FACE",FACE,{"disambiguationData":[OSD([subQ0])]}),makeQuery(id+"F4.opExtrude","SWEPT_FACE",FACE,{"disambiguationData":[OSD([subQ0])]})]})]})],"blendedInto":[]})]),OD(0.0)]})])]}),makeQuery(id+"F28.opExtrude","SWEPT_FACE",FACE,{"disambiguationData":[OSD([sQuery(id+"F27.wireOp",EDGE,"E79.left")])]})]});}
            var Q1;
            {var subQ0=sQuery(id+"F0.wireOp",EDGE,"E1.top");var subQ1=sQuery(id+"F0.wireOp",EDGE,"E4");var subQ2=sQuery(id+"F9.wireOp",EDGE,"E34");Q1=makeQuery(id+"F28.boolean.opBoolean","INTERSECT",EDGE,{"derivedFrom":[makeQuery(id+"F17.opShell","OFFSET_FACE",FACE,{"disambiguationData":[OSD([subQ0,subQ1,subQ2]),TDD([makeQuery(id+"F16.opFillet","BLEND_FACE",FACE,{"disambiguationData":[OSD([subQ0,subQ1,subQ2]),TDD([makeQuery(id+"F15.opFillet","BLEND_EDGE",EDGE,{"blendedFrom":[makeQuery(id+"F12.opFillet","BLEND_EDGE",EDGE,{"blendedFrom":[makeQuery(id+"F11.opExtrude","CAP_EDGE",EDGE,{"disambiguationData":[OSD([subQ2])],"isStart":true}),makeQuery(id+"F4.boolean.opBoolean","MERGE",FACE,{"derivedFrom":[makeQuery(id+"F3.opExtrude","SWEPT_FACE",FACE,{"disambiguationData":[OSD([subQ1])]}),makeQuery(id+"F4.opExtrude","SWEPT_FACE",FACE,{"disambiguationData":[OSD([subQ1])]})]})],"blendedInto":[makeQuery(id+"F4.boolean.opBoolean","MERGE",FACE,{"derivedFrom":[makeQuery(id+"F3.opExtrude","SWEPT_FACE",FACE,{"disambiguationData":[OSD([subQ1])]}),makeQuery(id+"F4.opExtrude","SWEPT_FACE",FACE,{"disambiguationData":[OSD([subQ1])]})]})]}),makeQuery(id+"F4.boolean.opBoolean","MERGE",FACE,{"derivedFrom":[makeQuery(id+"F3.opExtrude","SWEPT_FACE",FACE,{"disambiguationData":[OSD([subQ0])]}),makeQuery(id+"F4.opExtrude","SWEPT_FACE",FACE,{"disambiguationData":[OSD([subQ0])]})]})],"blendedInto":[makeQuery(id+"F4.boolean.opBoolean","MERGE",FACE,{"derivedFrom":[makeQuery(id+"F3.opExtrude","SWEPT_FACE",FACE,{"disambiguationData":[OSD([subQ0])]}),makeQuery(id+"F4.opExtrude","SWEPT_FACE",FACE,{"disambiguationData":[OSD([subQ0])]})]})]})]),OD(0.0)]})])]}),makeQuery(id+"F28.opExtrude","SWEPT_FACE",FACE,{"disambiguationData":[OSD([sQuery(id+"F27.wireOp",EDGE,"E75.left")])]})]});}
            var Q2;
            {var subQ0=sQuery(id+"F0.wireOp",EDGE,"E0.left");var subQ1=sQuery(id+"F9.wireOp",EDGE,"E34");var subQ2=makeQuery(id+"F11.opExtrude","CAP_EDGE",EDGE,{"disambiguationData":[OSD([subQ1])],"isStart":false});var subQ3=sQuery(id+"F0.wireOp",EDGE,"E4");Q2=makeQuery(id+"F28.boolean.opBoolean","INTERSECT",EDGE,{"derivedFrom":[makeQuery(id+"F17.opShell","OFFSET_FACE",FACE,{"disambiguationData":[OSD([subQ0,subQ3,subQ1]),TDD([makeQuery(id+"F16.opFillet","BLEND_FACE",FACE,{"disambiguationData":[OSD([subQ0,subQ3,subQ1]),TDD([makeQuery(id+"F15.opFillet","BLEND_EDGE",EDGE,{"blendedFrom":[makeQuery(id+"F12.opFillet","BLEND_EDGE",EDGE,{"blendedFrom":[subQ2,makeQuery(id+"F4.boolean.opBoolean","MERGE",FACE,{"derivedFrom":[makeQuery(id+"F3.opExtrude","SWEPT_FACE",FACE,{"disambiguationData":[OSD([subQ3])]}),makeQuery(id+"F4.opExtrude","SWEPT_FACE",FACE,{"disambiguationData":[OSD([subQ3])]})]})],"blendedInto":[makeQuery(id+"F4.boolean.opBoolean","MERGE",FACE,{"derivedFrom":[makeQuery(id+"F3.opExtrude","SWEPT_FACE",FACE,{"disambiguationData":[OSD([subQ3])]}),makeQuery(id+"F4.opExtrude","SWEPT_FACE",FACE,{"disambiguationData":[OSD([subQ3])]})]})]}),makeQuery(id+"F12.opFillet","BLEND_EDGE",EDGE,{"blendedFrom":[subQ2,makeQuery(id+"F4.boolean.opBoolean","MERGE",FACE,{"derivedFrom":[makeQuery(id+"F3.opExtrude","SWEPT_FACE",FACE,{"disambiguationData":[OSD([subQ0])]}),makeQuery(id+"F4.opExtrude","SWEPT_FACE",FACE,{"disambiguationData":[OSD([subQ0])]})]})],"blendedInto":[makeQuery(id+"F4.boolean.opBoolean","MERGE",FACE,{"derivedFrom":[makeQuery(id+"F3.opExtrude","SWEPT_FACE",FACE,{"disambiguationData":[OSD([subQ0])]}),makeQuery(id+"F4.opExtrude","SWEPT_FACE",FACE,{"disambiguationData":[OSD([subQ0])]})]})]})],"blendedInto":[]})]),OD(0.0)]})])]}),makeQuery(id+"F28.opExtrude","SWEPT_FACE",FACE,{"disambiguationData":[OSD([sQuery(id+"F27.wireOp",EDGE,"E80.bottom")])]})]});}
            var Q3;
            {var subQ0=sQuery(id+"F0.wireOp",EDGE,"E0.left");var subQ1=sQuery(id+"F0.wireOp",EDGE,"E3");var subQ2=sQuery(id+"F8.wireOp",EDGE,"E32");Q3=makeQuery(id+"F28.boolean.opBoolean","INTERSECT",EDGE,{"derivedFrom":[makeQuery(id+"F17.opShell","OFFSET_FACE",FACE,{"disambiguationData":[OSD([subQ0,subQ1,subQ2]),TDD([makeQuery(id+"F16.opFillet","BLEND_FACE",FACE,{"disambiguationData":[OSD([subQ0,subQ1,subQ2]),TDD([makeQuery(id+"F15.opFillet","BLEND_EDGE",EDGE,{"blendedFrom":[makeQuery(id+"F12.opFillet","BLEND_EDGE",EDGE,{"blendedFrom":[makeQuery(id+"F10.opExtrude","CAP_EDGE",EDGE,{"disambiguationData":[OSD([subQ2])],"isStart":true}),makeQuery(id+"F4.boolean.opBoolean","MERGE",FACE,{"derivedFrom":[makeQuery(id+"F3.opExtrude","SWEPT_FACE",FACE,{"disambiguationData":[OSD([subQ1])]}),makeQuery(id+"F4.opExtrude","SWEPT_FACE",FACE,{"disambiguationData":[OSD([subQ1])]})]})],"blendedInto":[makeQuery(id+"F4.boolean.opBoolean","MERGE",FACE,{"derivedFrom":[makeQuery(id+"F3.opExtrude","SWEPT_FACE",FACE,{"disambiguationData":[OSD([subQ1])]}),makeQuery(id+"F4.opExtrude","SWEPT_FACE",FACE,{"disambiguationData":[OSD([subQ1])]})]})]}),makeQuery(id+"F4.boolean.opBoolean","MERGE",FACE,{"derivedFrom":[makeQuery(id+"F3.opExtrude","SWEPT_FACE",FACE,{"disambiguationData":[OSD([subQ0])]}),makeQuery(id+"F4.opExtrude","SWEPT_FACE",FACE,{"disambiguationData":[OSD([subQ0])]})]})],"blendedInto":[makeQuery(id+"F4.boolean.opBoolean","MERGE",FACE,{"derivedFrom":[makeQuery(id+"F3.opExtrude","SWEPT_FACE",FACE,{"disambiguationData":[OSD([subQ0])]}),makeQuery(id+"F4.opExtrude","SWEPT_FACE",FACE,{"disambiguationData":[OSD([subQ0])]})]})]})]),OD(0.0)]})])]}),makeQuery(id+"F28.opExtrude","SWEPT_FACE",FACE,{"disambiguationData":[OSD([sQuery(id+"F27.wireOp",EDGE,"E74.bottom")])]})]});}
            var Q4;
            {var subQ0=sQuery(id+"F0.wireOp",EDGE,"E1.bottom");var subQ1=sQuery(id+"F8.wireOp",EDGE,"E32");var subQ2=makeQuery(id+"F10.opExtrude","CAP_EDGE",EDGE,{"disambiguationData":[OSD([subQ1])],"isStart":false});var subQ3=sQuery(id+"F0.wireOp",EDGE,"E3");Q4=makeQuery(id+"F28.boolean.opBoolean","INTERSECT",EDGE,{"derivedFrom":[makeQuery(id+"F17.opShell","OFFSET_FACE",FACE,{"disambiguationData":[OSD([subQ0,subQ3,subQ1]),TDD([makeQuery(id+"F16.opFillet","BLEND_FACE",FACE,{"disambiguationData":[OSD([subQ0,subQ3,subQ1]),TDD([makeQuery(id+"F15.opFillet","BLEND_EDGE",EDGE,{"blendedFrom":[makeQuery(id+"F12.opFillet","BLEND_EDGE",EDGE,{"blendedFrom":[subQ2,makeQuery(id+"F4.boolean.opBoolean","MERGE",FACE,{"derivedFrom":[makeQuery(id+"F3.opExtrude","SWEPT_FACE",FACE,{"disambiguationData":[OSD([subQ3])]}),makeQuery(id+"F4.opExtrude","SWEPT_FACE",FACE,{"disambiguationData":[OSD([subQ3])]})]})],"blendedInto":[makeQuery(id+"F4.boolean.opBoolean","MERGE",FACE,{"derivedFrom":[makeQuery(id+"F3.opExtrude","SWEPT_FACE",FACE,{"disambiguationData":[OSD([subQ3])]}),makeQuery(id+"F4.opExtrude","SWEPT_FACE",FACE,{"disambiguationData":[OSD([subQ3])]})]})]}),makeQuery(id+"F12.opFillet","BLEND_EDGE",EDGE,{"blendedFrom":[subQ2,makeQuery(id+"F4.boolean.opBoolean","MERGE",FACE,{"derivedFrom":[makeQuery(id+"F3.opExtrude","SWEPT_FACE",FACE,{"disambiguationData":[OSD([subQ0])]}),makeQuery(id+"F4.opExtrude","SWEPT_FACE",FACE,{"disambiguationData":[OSD([subQ0])]})]})],"blendedInto":[makeQuery(id+"F4.boolean.opBoolean","MERGE",FACE,{"derivedFrom":[makeQuery(id+"F3.opExtrude","SWEPT_FACE",FACE,{"disambiguationData":[OSD([subQ0])]}),makeQuery(id+"F4.opExtrude","SWEPT_FACE",FACE,{"disambiguationData":[OSD([subQ0])]})]})]})],"blendedInto":[]})]),OD(0.0)]})])]}),makeQuery(id+"F28.opExtrude","SWEPT_FACE",FACE,{"disambiguationData":[OSD([sQuery(id+"F27.wireOp",EDGE,"E76.left")])]})]});}
            var Q5;
            {var subQ0=sQuery(id+"F0.wireOp",EDGE,"E0.right");var subQ1=sQuery(id+"F9.wireOp",EDGE,"E35");var subQ2=makeQuery(id+"F11.opExtrude","CAP_EDGE",EDGE,{"disambiguationData":[OSD([subQ1])],"isStart":true});var subQ3=sQuery(id+"F0.wireOp",EDGE,"E2");Q5=makeQuery(id+"F28.boolean.opBoolean","INTERSECT",EDGE,{"derivedFrom":[makeQuery(id+"F17.opShell","OFFSET_FACE",FACE,{"disambiguationData":[OSD([subQ0,subQ3,subQ1]),TDD([makeQuery(id+"F16.opFillet","BLEND_FACE",FACE,{"disambiguationData":[OSD([subQ0,subQ3,subQ1]),TDD([makeQuery(id+"F15.opFillet","BLEND_EDGE",EDGE,{"blendedFrom":[makeQuery(id+"F12.opFillet","BLEND_EDGE",EDGE,{"blendedFrom":[subQ2,makeQuery(id+"F4.boolean.opBoolean","MERGE",FACE,{"derivedFrom":[makeQuery(id+"F3.opExtrude","SWEPT_FACE",FACE,{"disambiguationData":[OSD([subQ3])]}),makeQuery(id+"F4.opExtrude","SWEPT_FACE",FACE,{"disambiguationData":[OSD([subQ3])]})]})],"blendedInto":[makeQuery(id+"F4.boolean.opBoolean","MERGE",FACE,{"derivedFrom":[makeQuery(id+"F3.opExtrude","SWEPT_FACE",FACE,{"disambiguationData":[OSD([subQ3])]}),makeQuery(id+"F4.opExtrude","SWEPT_FACE",FACE,{"disambiguationData":[OSD([subQ3])]})]})]}),makeQuery(id+"F12.opFillet","BLEND_EDGE",EDGE,{"blendedFrom":[subQ2,makeQuery(id+"F4.boolean.opBoolean","MERGE",FACE,{"derivedFrom":[makeQuery(id+"F3.opExtrude","SWEPT_FACE",FACE,{"disambiguationData":[OSD([subQ0])]}),makeQuery(id+"F4.opExtrude","SWEPT_FACE",FACE,{"disambiguationData":[OSD([subQ0])]})]})],"blendedInto":[makeQuery(id+"F4.boolean.opBoolean","MERGE",FACE,{"derivedFrom":[makeQuery(id+"F3.opExtrude","SWEPT_FACE",FACE,{"disambiguationData":[OSD([subQ0])]}),makeQuery(id+"F4.opExtrude","SWEPT_FACE",FACE,{"disambiguationData":[OSD([subQ0])]})]})]})],"blendedInto":[]})]),OD(0.0)]})])]}),makeQuery(id+"F28.opExtrude","SWEPT_FACE",FACE,{"disambiguationData":[OSD([sQuery(id+"F27.wireOp",EDGE,"E78.top")])]})]});}
            var Q6;
            {var subQ0=sQuery(id+"F0.wireOp",EDGE,"E1.bottom");var subQ1=sQuery(id+"F0.wireOp",EDGE,"E2");var subQ2=sQuery(id+"F9.wireOp",EDGE,"E35");Q6=makeQuery(id+"F28.boolean.opBoolean","INTERSECT",EDGE,{"derivedFrom":[makeQuery(id+"F17.opShell","OFFSET_FACE",FACE,{"disambiguationData":[OSD([subQ0,subQ1,subQ2]),TDD([makeQuery(id+"F16.opFillet","BLEND_FACE",FACE,{"disambiguationData":[OSD([subQ0,subQ1,subQ2]),TDD([makeQuery(id+"F15.opFillet","BLEND_EDGE",EDGE,{"blendedFrom":[makeQuery(id+"F12.opFillet","BLEND_EDGE",EDGE,{"blendedFrom":[makeQuery(id+"F11.opExtrude","CAP_EDGE",EDGE,{"disambiguationData":[OSD([subQ2])],"isStart":false}),makeQuery(id+"F4.boolean.opBoolean","MERGE",FACE,{"derivedFrom":[makeQuery(id+"F3.opExtrude","SWEPT_FACE",FACE,{"disambiguationData":[OSD([subQ1])]}),makeQuery(id+"F4.opExtrude","SWEPT_FACE",FACE,{"disambiguationData":[OSD([subQ1])]})]})],"blendedInto":[makeQuery(id+"F4.boolean.opBoolean","MERGE",FACE,{"derivedFrom":[makeQuery(id+"F3.opExtrude","SWEPT_FACE",FACE,{"disambiguationData":[OSD([subQ1])]}),makeQuery(id+"F4.opExtrude","SWEPT_FACE",FACE,{"disambiguationData":[OSD([subQ1])]})]})]}),makeQuery(id+"F4.boolean.opBoolean","MERGE",FACE,{"derivedFrom":[makeQuery(id+"F3.opExtrude","SWEPT_FACE",FACE,{"disambiguationData":[OSD([subQ0])]}),makeQuery(id+"F4.opExtrude","SWEPT_FACE",FACE,{"disambiguationData":[OSD([subQ0])]})]})],"blendedInto":[makeQuery(id+"F4.boolean.opBoolean","MERGE",FACE,{"derivedFrom":[makeQuery(id+"F3.opExtrude","SWEPT_FACE",FACE,{"disambiguationData":[OSD([subQ0])]}),makeQuery(id+"F4.opExtrude","SWEPT_FACE",FACE,{"disambiguationData":[OSD([subQ0])]})]})]})]),OD(0.0)]})])]}),makeQuery(id+"F28.opExtrude","SWEPT_FACE",FACE,{"disambiguationData":[OSD([sQuery(id+"F27.wireOp",EDGE,"E77.left")])]})]});}
            var Q7;
            {var subQ0=sQuery(id+"F0.wireOp",EDGE,"E0.right");var subQ1=sQuery(id+"F0.wireOp",EDGE,"E5");var subQ2=sQuery(id+"F8.wireOp",EDGE,"E30");Q7=makeQuery(id+"F28.boolean.opBoolean","INTERSECT",EDGE,{"derivedFrom":[makeQuery(id+"F17.opShell","OFFSET_FACE",FACE,{"disambiguationData":[OSD([subQ0,subQ1,subQ2]),TDD([makeQuery(id+"F16.opFillet","BLEND_FACE",FACE,{"disambiguationData":[OSD([subQ0,subQ1,subQ2]),TDD([makeQuery(id+"F15.opFillet","BLEND_EDGE",EDGE,{"blendedFrom":[makeQuery(id+"F12.opFillet","BLEND_EDGE",EDGE,{"blendedFrom":[makeQuery(id+"F10.opExtrude","CAP_EDGE",EDGE,{"disambiguationData":[OSD([subQ2])],"isStart":false}),makeQuery(id+"F4.boolean.opBoolean","MERGE",FACE,{"derivedFrom":[makeQuery(id+"F3.opExtrude","SWEPT_FACE",FACE,{"disambiguationData":[OSD([subQ1])]}),makeQuery(id+"F4.opExtrude","SWEPT_FACE",FACE,{"disambiguationData":[OSD([subQ1])]})]})],"blendedInto":[makeQuery(id+"F4.boolean.opBoolean","MERGE",FACE,{"derivedFrom":[makeQuery(id+"F3.opExtrude","SWEPT_FACE",FACE,{"disambiguationData":[OSD([subQ1])]}),makeQuery(id+"F4.opExtrude","SWEPT_FACE",FACE,{"disambiguationData":[OSD([subQ1])]})]})]}),makeQuery(id+"F4.boolean.opBoolean","MERGE",FACE,{"derivedFrom":[makeQuery(id+"F3.opExtrude","SWEPT_FACE",FACE,{"disambiguationData":[OSD([subQ0])]}),makeQuery(id+"F4.opExtrude","SWEPT_FACE",FACE,{"disambiguationData":[OSD([subQ0])]})]})],"blendedInto":[makeQuery(id+"F4.boolean.opBoolean","MERGE",FACE,{"derivedFrom":[makeQuery(id+"F3.opExtrude","SWEPT_FACE",FACE,{"disambiguationData":[OSD([subQ0])]}),makeQuery(id+"F4.opExtrude","SWEPT_FACE",FACE,{"disambiguationData":[OSD([subQ0])]})]})]})]),OD(0.0)]})])]}),makeQuery(id+"F28.opExtrude","SWEPT_FACE",FACE,{"disambiguationData":[OSD([sQuery(id+"F27.wireOp",EDGE,"E88.bottom")])]})]});}
            fillet(context, id + "F33", {"entities" : qUnion([Q0, Q1, Q2, Q3, Q4, Q5, Q6, Q7]), "radius" : 2.03 * mm, "tangentPropagation" : true, "allowEdgeOverflow" : false});
        }
        {
            var Q0;
            Q0=makeQuery(id+"F26.boolean.opBoolean","MERGE",FACE,{"derivedFrom":[makeQuery(id+"F19.boolean.opBoolean","COPY",FACE,{"derivedFrom":makeQuery(id+"F19.opExtrude","SWEPT_FACE",FACE,{"disambiguationData":[OSD([sQuery(id+"F18.wireOp",EDGE,"E38.bottom")])]})}),makeQuery(id+"F26.opExtrude","CAP_FACE",FACE,{"disambiguationData":[OSD([sQuery(id+"F25.wireOp",EDGE,"E42"),sQuery(id+"F25.wireOp",EDGE,"E49"),sQuery(id+"F25.wireOp",EDGE,"E56.bottom"),sQuery(id+"F25.wireOp",EDGE,"E56.left"),sQuery(id+"F25.wireOp",EDGE,"E56.right"),sQuery(id+"F25.wireOp",EDGE,"E68")])],"isStart":true}),makeQuery(id+"F26.opExtrude","CAP_FACE",FACE,{"disambiguationData":[OSD([sQuery(id+"F25.wireOp",EDGE,"E43"),sQuery(id+"F25.wireOp",EDGE,"E50"),sQuery(id+"F25.wireOp",EDGE,"E57.bottom"),sQuery(id+"F25.wireOp",EDGE,"E57.left"),sQuery(id+"F25.wireOp",EDGE,"E57.right"),sQuery(id+"F25.wireOp",EDGE,"E67")])],"isStart":true}),makeQuery(id+"F26.opExtrude","CAP_FACE",FACE,{"disambiguationData":[OSD([sQuery(id+"F25.wireOp",EDGE,"E44"),sQuery(id+"F25.wireOp",EDGE,"E51"),sQuery(id+"F25.wireOp",EDGE,"E58.bottom"),sQuery(id+"F25.wireOp",EDGE,"E58.top"),sQuery(id+"F25.wireOp",EDGE,"E58.left"),sQuery(id+"F25.wireOp",EDGE,"E66")])],"isStart":true}),makeQuery(id+"F26.opExtrude","CAP_FACE",FACE,{"disambiguationData":[OSD([sQuery(id+"F25.wireOp",EDGE,"E45"),sQuery(id+"F25.wireOp",EDGE,"E52"),sQuery(id+"F25.wireOp",EDGE,"E59.bottom"),sQuery(id+"F25.wireOp",EDGE,"E59.top"),sQuery(id+"F25.wireOp",EDGE,"E59.left"),sQuery(id+"F25.wireOp",EDGE,"E65")])],"isStart":true}),makeQuery(id+"F26.opExtrude","CAP_FACE",FACE,{"disambiguationData":[OSD([sQuery(id+"F25.wireOp",EDGE,"E46"),sQuery(id+"F25.wireOp",EDGE,"E53"),sQuery(id+"F25.wireOp",EDGE,"E60.top"),sQuery(id+"F25.wireOp",EDGE,"E60.left"),sQuery(id+"F25.wireOp",EDGE,"E60.right"),sQuery(id+"F25.wireOp",EDGE,"E63")])],"isStart":true}),makeQuery(id+"F26.opExtrude","CAP_FACE",FACE,{"disambiguationData":[OSD([sQuery(id+"F25.wireOp",EDGE,"E47"),sQuery(id+"F25.wireOp",EDGE,"E54"),sQuery(id+"F25.wireOp",EDGE,"E61.top"),sQuery(id+"F25.wireOp",EDGE,"E61.left"),sQuery(id+"F25.wireOp",EDGE,"E61.right"),sQuery(id+"F25.wireOp",EDGE,"E64")])],"isStart":true}),makeQuery(id+"F26.opExtrude","CAP_FACE",FACE,{"disambiguationData":[OSD([sQuery(id+"F25.wireOp",EDGE,"E48"),sQuery(id+"F25.wireOp",EDGE,"E55"),sQuery(id+"F25.wireOp",EDGE,"E62.bottom"),sQuery(id+"F25.wireOp",EDGE,"E62.top"),sQuery(id+"F25.wireOp",EDGE,"E62.right"),sQuery(id+"F25.wireOp",EDGE,"E69")])],"isStart":true})]});
            var Q1;
            Q1=makeQuery(id+"F30.boolean.opBoolean","COPY",FACE,{"derivedFrom":makeQuery(id+"F30.opExtrude","SWEPT_FACE",FACE,{"disambiguationData":[OSD([sQuery(id+"F29.wireOp",EDGE,"E90.bottom")])]})});
            fillet(context, id + "F34", {"entities" : qUnion([Q0, Q1]), "radius" : 0.25 * mm, "tangentPropagation" : true, "allowEdgeOverflow" : false});
        }
        {
            var Q0;
            {var subQ0=sQuery(id+"F25.wireOp",EDGE,"E49");Q0=makeQuery(id+"F26.opExtrude","CAP_EDGE",EDGE,{"disambiguationData":[OSD([subQ0]),TDD([makeQuery(id+"F25.imprint","IMPRINT",EDGE,{"disambiguationData":[TD([[makeQuery(id+"F25.imprint","INTERSECT",VERTEX,{"derivedFrom":[subQ0,sQuery(id+"F25.wireOp",EDGE,"E56.right")]}),-1.0]])],"derivedFrom":subQ0}),makeQuery(id+"F25.imprint","IMPRINT",EDGE,{"disambiguationData":[TD([[makeQuery(id+"F25.imprint","INTERSECT",VERTEX,{"derivedFrom":[subQ0,sQuery(id+"F25.wireOp",EDGE,"E56.left")]}),1.0]])],"derivedFrom":subQ0})])],"isStart":false});}
            var Q1;
            Q1=makeQuery(id+"F26.opExtrude","CAP_EDGE",EDGE,{"disambiguationData":[OSD([sQuery(id+"F25.wireOp",EDGE,"E42")])],"isStart":false});
            var Q2;
            {var subQ0=sQuery(id+"F25.wireOp",EDGE,"E42");Q2=makeQuery(id+"F32.opFillet","BLEND_EDGE",EDGE,{"blendedFrom":[makeQuery(id+"F26.boolean.opBoolean","INTERSECT",EDGE,{"derivedFrom":[makeQuery(id+"F17.opShell","OFFSET_FACE",FACE,{"disambiguationData":[OSD([sQuery(id+"F0.wireOp",EDGE,"E1.bottom"),sQuery(id+"F2.wireOp",EDGE,"E8"),sQuery(id+"F9.wireOp",EDGE,"E35")])]}),makeQuery(id+"F26.opExtrude","CAP_FACE",FACE,{"disambiguationData":[OSD([subQ0,sQuery(id+"F25.wireOp",EDGE,"E49"),sQuery(id+"F25.wireOp",EDGE,"E56.bottom"),sQuery(id+"F25.wireOp",EDGE,"E56.left"),sQuery(id+"F25.wireOp",EDGE,"E56.right"),sQuery(id+"F25.wireOp",EDGE,"E68")])],"isStart":false})]}),makeQuery(id+"F26.opExtrude","SWEPT_FACE",FACE,{"disambiguationData":[OSD([subQ0])]})],"blendedInto":[makeQuery(id+"F26.opExtrude","SWEPT_FACE",FACE,{"disambiguationData":[OSD([subQ0])]})]});}
            var Q3;
            Q3=makeQuery(id+"F26.opExtrude","CAP_EDGE",EDGE,{"disambiguationData":[OSD([sQuery(id+"F25.wireOp",EDGE,"E48")])],"isStart":false});
            var Q4;
            {var subQ0=sQuery(id+"F25.wireOp",EDGE,"E55");var subQ1=makeQuery(id+"F25.imprint","INTERSECT",VERTEX,{"derivedFrom":[subQ0,sQuery(id+"F25.wireOp",EDGE,"E62.left")]});Q4=makeQuery(id+"F26.opExtrude","CAP_EDGE",EDGE,{"disambiguationData":[OSD([subQ0]),TDD([makeQuery(id+"F25.imprint","IMPRINT",EDGE,{"disambiguationData":[TD([[makeQuery(id+"F25.imprint","INTERSECT",VERTEX,{"derivedFrom":[subQ0,sQuery(id+"F25.wireOp",EDGE,"E62.bottom")]}),1.0]])],"derivedFrom":subQ0}),makeQuery(id+"F25.imprint","IMPRINT",EDGE,{"disambiguationData":[TD([[subQ1,1.0]])],"derivedFrom":subQ0})])],"isStart":false});}
            var Q5;
            Q5=makeQuery(id+"F26.opExtrude","CAP_EDGE",EDGE,{"disambiguationData":[OSD([sQuery(id+"F25.wireOp",EDGE,"E43")])],"isStart":false});
            var Q6;
            {var subQ0=sQuery(id+"F25.wireOp",EDGE,"E50");Q6=makeQuery(id+"F26.opExtrude","CAP_EDGE",EDGE,{"disambiguationData":[OSD([subQ0]),TDD([makeQuery(id+"F25.imprint","IMPRINT",EDGE,{"disambiguationData":[TD([[makeQuery(id+"F25.imprint","INTERSECT",VERTEX,{"derivedFrom":[subQ0,sQuery(id+"F25.wireOp",EDGE,"E57.right")]}),-1.0]])],"derivedFrom":subQ0}),makeQuery(id+"F25.imprint","IMPRINT",EDGE,{"disambiguationData":[TD([[makeQuery(id+"F25.imprint","INTERSECT",VERTEX,{"derivedFrom":[subQ0,sQuery(id+"F25.wireOp",EDGE,"E57.left")]}),1.0]])],"derivedFrom":subQ0})])],"isStart":false});}
            var Q7;
            {var subQ0=sQuery(id+"F25.wireOp",EDGE,"E51");var subQ1=makeQuery(id+"F25.imprint","INTERSECT",VERTEX,{"derivedFrom":[subQ0,sQuery(id+"F25.wireOp",EDGE,"E58.right")]});Q7=makeQuery(id+"F26.opExtrude","CAP_EDGE",EDGE,{"disambiguationData":[OSD([subQ0]),TDD([makeQuery(id+"F25.imprint","IMPRINT",EDGE,{"disambiguationData":[TD([[makeQuery(id+"F25.imprint","INTERSECT",VERTEX,{"derivedFrom":[subQ0,sQuery(id+"F25.wireOp",EDGE,"E58.bottom")]}),-1.0]])],"derivedFrom":subQ0}),makeQuery(id+"F25.imprint","IMPRINT",EDGE,{"disambiguationData":[TD([[subQ1,-1.0]])],"derivedFrom":subQ0})])],"isStart":false});}
            var Q8;
            Q8=makeQuery(id+"F26.opExtrude","CAP_EDGE",EDGE,{"disambiguationData":[OSD([sQuery(id+"F25.wireOp",EDGE,"E44")])],"isStart":false});
            var Q9;
            {var subQ0=sQuery(id+"F25.wireOp",EDGE,"E54");var subQ1=makeQuery(id+"F25.imprint","INTERSECT",VERTEX,{"derivedFrom":[subQ0,sQuery(id+"F25.wireOp",EDGE,"E61.bottom")]});Q9=makeQuery(id+"F26.opExtrude","CAP_EDGE",EDGE,{"disambiguationData":[OSD([subQ0]),TDD([makeQuery(id+"F25.imprint","IMPRINT",EDGE,{"disambiguationData":[TD([[subQ1,1.0]])],"derivedFrom":subQ0}),makeQuery(id+"F25.imprint","IMPRINT",EDGE,{"disambiguationData":[TD([[subQ1,-1.0]])],"derivedFrom":subQ0})])],"isStart":false});}
            var Q10;
            Q10=makeQuery(id+"F26.opExtrude","CAP_EDGE",EDGE,{"disambiguationData":[OSD([sQuery(id+"F25.wireOp",EDGE,"E47")])],"isStart":false});
            var Q11;
            {var subQ0=sQuery(id+"F25.wireOp",EDGE,"E53");var subQ1=makeQuery(id+"F25.imprint","INTERSECT",VERTEX,{"derivedFrom":[subQ0,sQuery(id+"F25.wireOp",EDGE,"E60.bottom")]});Q11=makeQuery(id+"F26.opExtrude","CAP_EDGE",EDGE,{"disambiguationData":[OSD([subQ0]),TDD([makeQuery(id+"F25.imprint","IMPRINT",EDGE,{"disambiguationData":[TD([[subQ1,1.0]])],"derivedFrom":subQ0}),makeQuery(id+"F25.imprint","IMPRINT",EDGE,{"disambiguationData":[TD([[subQ1,-1.0]])],"derivedFrom":subQ0})])],"isStart":false});}
            var Q12;
            Q12=makeQuery(id+"F26.opExtrude","CAP_EDGE",EDGE,{"disambiguationData":[OSD([sQuery(id+"F25.wireOp",EDGE,"E46")])],"isStart":false});
            var Q13;
            {var subQ0=sQuery(id+"F25.wireOp",EDGE,"E52");var subQ1=makeQuery(id+"F25.imprint","INTERSECT",VERTEX,{"derivedFrom":[subQ0,sQuery(id+"F25.wireOp",EDGE,"E59.right")]});Q13=makeQuery(id+"F26.opExtrude","CAP_EDGE",EDGE,{"disambiguationData":[OSD([subQ0]),TDD([makeQuery(id+"F25.imprint","IMPRINT",EDGE,{"disambiguationData":[TD([[makeQuery(id+"F25.imprint","INTERSECT",VERTEX,{"derivedFrom":[subQ0,sQuery(id+"F25.wireOp",EDGE,"E59.bottom")]}),-1.0]])],"derivedFrom":subQ0}),makeQuery(id+"F25.imprint","IMPRINT",EDGE,{"disambiguationData":[TD([[subQ1,-1.0]])],"derivedFrom":subQ0})])],"isStart":false});}
            var Q14;
            Q14=makeQuery(id+"F26.opExtrude","CAP_EDGE",EDGE,{"disambiguationData":[OSD([sQuery(id+"F25.wireOp",EDGE,"E45")])],"isStart":false});
            var Q15;
            {var subQ0=sQuery(id+"F27.wireOp",EDGE,"E88.bottom");var subQ1=sQuery(id+"F0.wireOp",EDGE,"E0.right");var subQ2=sQuery(id+"F0.wireOp",EDGE,"E5");var subQ3=sQuery(id+"F8.wireOp",EDGE,"E30");Q15=makeQuery(id+"F33.opFillet","BLEND_EDGE",EDGE,{"blendedFrom":[makeQuery(id+"F28.boolean.opBoolean","INTERSECT",EDGE,{"derivedFrom":[makeQuery(id+"F17.opShell","OFFSET_FACE",FACE,{"disambiguationData":[OSD([subQ1,subQ2,subQ3]),TDD([makeQuery(id+"F16.opFillet","BLEND_FACE",FACE,{"disambiguationData":[OSD([subQ1,subQ2,subQ3]),TDD([makeQuery(id+"F15.opFillet","BLEND_EDGE",EDGE,{"blendedFrom":[makeQuery(id+"F12.opFillet","BLEND_EDGE",EDGE,{"blendedFrom":[makeQuery(id+"F10.opExtrude","CAP_EDGE",EDGE,{"disambiguationData":[OSD([subQ3])],"isStart":false}),makeQuery(id+"F4.boolean.opBoolean","MERGE",FACE,{"derivedFrom":[makeQuery(id+"F3.opExtrude","SWEPT_FACE",FACE,{"disambiguationData":[OSD([subQ2])]}),makeQuery(id+"F4.opExtrude","SWEPT_FACE",FACE,{"disambiguationData":[OSD([subQ2])]})]})],"blendedInto":[makeQuery(id+"F4.boolean.opBoolean","MERGE",FACE,{"derivedFrom":[makeQuery(id+"F3.opExtrude","SWEPT_FACE",FACE,{"disambiguationData":[OSD([subQ2])]}),makeQuery(id+"F4.opExtrude","SWEPT_FACE",FACE,{"disambiguationData":[OSD([subQ2])]})]})]}),makeQuery(id+"F4.boolean.opBoolean","MERGE",FACE,{"derivedFrom":[makeQuery(id+"F3.opExtrude","SWEPT_FACE",FACE,{"disambiguationData":[OSD([subQ1])]}),makeQuery(id+"F4.opExtrude","SWEPT_FACE",FACE,{"disambiguationData":[OSD([subQ1])]})]})],"blendedInto":[makeQuery(id+"F4.boolean.opBoolean","MERGE",FACE,{"derivedFrom":[makeQuery(id+"F3.opExtrude","SWEPT_FACE",FACE,{"disambiguationData":[OSD([subQ1])]}),makeQuery(id+"F4.opExtrude","SWEPT_FACE",FACE,{"disambiguationData":[OSD([subQ1])]})]})]})]),OD(0.0)]})])]}),makeQuery(id+"F28.opExtrude","SWEPT_FACE",FACE,{"disambiguationData":[OSD([subQ0])]})]}),makeQuery(id+"F28.boolean.opBoolean","MERGE",FACE,{"derivedFrom":[makeQuery(id+"F26.opExtrude","CAP_FACE",FACE,{"disambiguationData":[OSD([sQuery(id+"F25.wireOp",EDGE,"E70"),sQuery(id+"F25.wireOp",EDGE,"E71"),sQuery(id+"F25.wireOp",EDGE,"E72.bottom"),sQuery(id+"F25.wireOp",EDGE,"E72.top"),sQuery(id+"F25.wireOp",EDGE,"E72.right"),sQuery(id+"F25.wireOp",EDGE,"E73")])],"isStart":false}),makeQuery(id+"F28.opExtrude","CAP_FACE",FACE,{"disambiguationData":[OSD([subQ0,sQuery(id+"F27.wireOp",EDGE,"E88.top"),sQuery(id+"F27.wireOp",EDGE,"E88.left"),sQuery(id+"F27.wireOp",EDGE,"E88.right"),sQuery(id+"F27.wireOp",EDGE,"E89")])],"isStart":true})]})],"blendedInto":[makeQuery(id+"F28.boolean.opBoolean","MERGE",FACE,{"derivedFrom":[makeQuery(id+"F26.opExtrude","CAP_FACE",FACE,{"disambiguationData":[OSD([sQuery(id+"F25.wireOp",EDGE,"E70"),sQuery(id+"F25.wireOp",EDGE,"E71"),sQuery(id+"F25.wireOp",EDGE,"E72.bottom"),sQuery(id+"F25.wireOp",EDGE,"E72.top"),sQuery(id+"F25.wireOp",EDGE,"E72.right"),sQuery(id+"F25.wireOp",EDGE,"E73")])],"isStart":false}),makeQuery(id+"F28.opExtrude","CAP_FACE",FACE,{"disambiguationData":[OSD([subQ0,sQuery(id+"F27.wireOp",EDGE,"E88.top"),sQuery(id+"F27.wireOp",EDGE,"E88.left"),sQuery(id+"F27.wireOp",EDGE,"E88.right"),sQuery(id+"F27.wireOp",EDGE,"E89")])],"isStart":true})]})]});}
            var Q16;
            Q16=makeQuery(id+"F30.boolean.opBoolean","INTERSECT",EDGE,{"disambiguationData":[OD(0.0)],"derivedFrom":[makeQuery(id+"F28.boolean.opBoolean","MERGE",FACE,{"derivedFrom":[makeQuery(id+"F26.opExtrude","CAP_FACE",FACE,{"disambiguationData":[OSD([sQuery(id+"F25.wireOp",EDGE,"E70"),sQuery(id+"F25.wireOp",EDGE,"E71"),sQuery(id+"F25.wireOp",EDGE,"E72.bottom"),sQuery(id+"F25.wireOp",EDGE,"E72.top"),sQuery(id+"F25.wireOp",EDGE,"E72.right"),sQuery(id+"F25.wireOp",EDGE,"E73")])],"isStart":false}),makeQuery(id+"F28.opExtrude","CAP_FACE",FACE,{"disambiguationData":[OSD([sQuery(id+"F27.wireOp",EDGE,"E88.bottom"),sQuery(id+"F27.wireOp",EDGE,"E88.top"),sQuery(id+"F27.wireOp",EDGE,"E88.left"),sQuery(id+"F27.wireOp",EDGE,"E88.right"),sQuery(id+"F27.wireOp",EDGE,"E89")])],"isStart":true})]}),makeQuery(id+"F30.opExtrude","SWEPT_FACE",FACE,{"disambiguationData":[OSD([sQuery(id+"F29.wireOp",EDGE,"E90.left")])]})]});
            var Q17;
            Q17=makeQuery(id+"F26.opExtrude","CAP_EDGE",EDGE,{"disambiguationData":[OSD([sQuery(id+"F25.wireOp",EDGE,"E71")])],"isStart":false});
            var Q18;
            {var subQ0=sQuery(id+"F25.wireOp",EDGE,"E71");Q18=makeQuery(id+"F34.opFillet","BLEND_EDGE",EDGE,{"blendedFrom":[makeQuery(id+"F30.boolean.opBoolean","INTERSECT",EDGE,{"disambiguationData":[OD(1.0)],"derivedFrom":[makeQuery(id+"F28.boolean.opBoolean","MERGE",FACE,{"derivedFrom":[makeQuery(id+"F26.opExtrude","CAP_FACE",FACE,{"disambiguationData":[OSD([sQuery(id+"F25.wireOp",EDGE,"E70"),subQ0,sQuery(id+"F25.wireOp",EDGE,"E72.bottom"),sQuery(id+"F25.wireOp",EDGE,"E72.top"),sQuery(id+"F25.wireOp",EDGE,"E72.right"),sQuery(id+"F25.wireOp",EDGE,"E73")])],"isStart":false}),makeQuery(id+"F28.opExtrude","CAP_FACE",FACE,{"disambiguationData":[OSD([sQuery(id+"F27.wireOp",EDGE,"E88.bottom"),sQuery(id+"F27.wireOp",EDGE,"E88.top"),sQuery(id+"F27.wireOp",EDGE,"E88.left"),sQuery(id+"F27.wireOp",EDGE,"E88.right"),sQuery(id+"F27.wireOp",EDGE,"E89")])],"isStart":true})]}),makeQuery(id+"F30.opExtrude","SWEPT_FACE",FACE,{"disambiguationData":[OSD([sQuery(id+"F29.wireOp",EDGE,"E90.left")])]})]}),makeQuery(id+"F26.opExtrude","SWEPT_FACE",FACE,{"disambiguationData":[OSD([subQ0])]})],"blendedInto":[makeQuery(id+"F26.opExtrude","SWEPT_FACE",FACE,{"disambiguationData":[OSD([subQ0])]})]});}
            fillet(context, id + "F35", {"entities" : qUnion([Q0, Q1, Q2, Q3, Q4, Q5, Q6, Q7, Q8, Q9, Q10, Q11, Q12, Q13, Q14, Q15, Q16, Q17, Q18]), "radius" : 0.38 * mm, "tangentPropagation" : true, "allowEdgeOverflow" : false});
        }
    });
